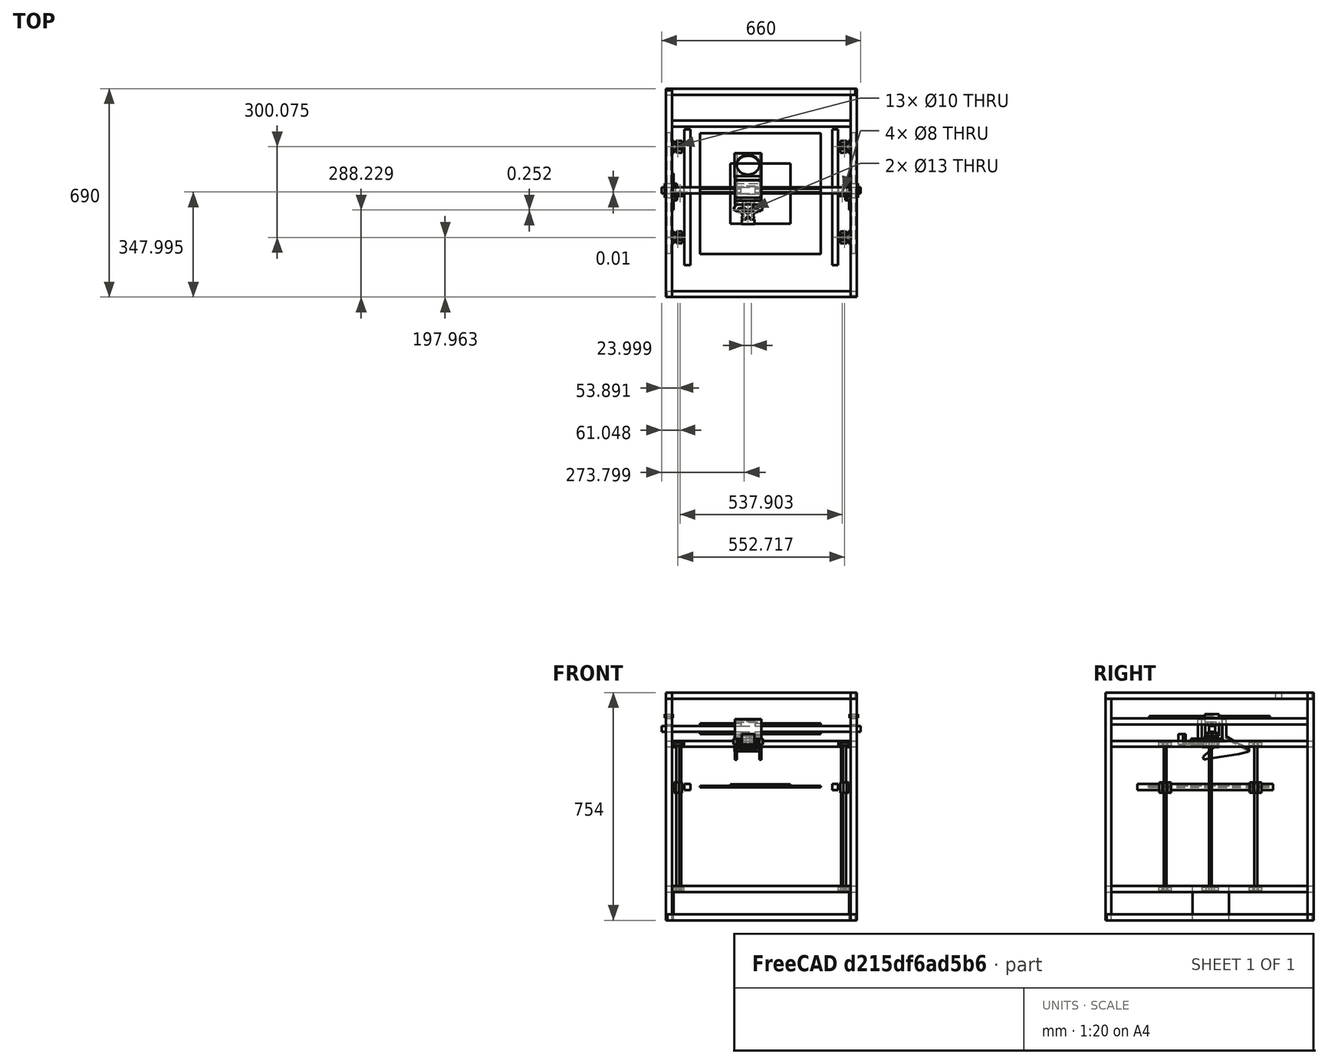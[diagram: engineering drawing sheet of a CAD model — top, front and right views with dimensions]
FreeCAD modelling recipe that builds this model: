
FCSTD DOCUMENT  (FreeCAD 0.17R13522 (Git))
Label: Frame_1
License: All rights reserved
LicenseURL: http://en.wikipedia.org/wiki/All_rights_reserved
objects: Part::Box×44, Sketcher::SketchObject×29, Part::Extrusion×29, Mesh::Feature×8, Part::Cylinder×6, Part::MultiFuse×3, App::DocumentObjectGroup×1
note: 111 computed .brp shape members not serialized (recipe doc carries the construction recipe); baked Part::Feature solids carry a one-line shape summary decoded from their .brp

FEATURE [Part::Box] Box017  label="Vslot Y Direito"
  AttacherType = Attacher::AttachEngine3D
  Height = 20
  Length = 20
  Placement = pos=(1268.5,175,-27.8) rot=(0,0,1;0rad)
  Width = 650
FEATURE [Part::Box] Box016  label="Vslot Y Esquerdo"
  AttacherType = Attacher::AttachEngine3D
  Height = 20
  Length = 20
  Placement = pos=(656,175,-27.8) rot=(0,0,1;0rad)
  Width = 650
FEATURE [Part::Box] Box020  label="Rail Y Esquerdo"
  AttacherType = Attacher::AttachEngine3D
  Height = 7.8
  Length = 12.2
  Placement = pos=(660,300,-7.8) rot=(0,0,1;0rad)
  Width = 400
FEATURE [Part::Box] Box021  label="Rail Y Direito"
  AttacherType = Attacher::AttachEngine3D
  Height = 7.8
  Length = 12.2
  Placement = pos=(1272.5,300,-7.8) rot=(0,0,1;0rad)
  Width = 400
FEATURE [Mesh::Feature] mgn12h_1  label="mgn12h_Esquerdo"
  Placement = pos=(690.5,535.45,17) rot=(-0.707107,0.707107,0;3.14159rad)
FEATURE [Mesh::Feature] mgn12h_002  label="mgn12h_Direito"
  Placement = pos=(1302,535.45,17) rot=(0.707107,-0.707107,0;3.14159rad)
FEATURE [Part::Box] Box005  label="Mgn12h y esquerdo"
  AttacherType = Attacher::AttachEngine3D
  Height = 13
  Length = 27.1
  Placement = pos=(652.5,484,-6) rot=(0,0,1;0rad)
  Width = 47.55
FEATURE [Part::Box] Box022  label="Mgn12h y direito"
  AttacherType = Attacher::AttachEngine3D
  Height = 13
  Length = 27.1
  Placement = pos=(1265,484,-6) rot=(0,0,1;0rad)
  Width = 47.55
FEATURE [Part::Box] Box  label="Vslot frontal esquerdo"
  AttacherType = Attacher::AttachEngine3D
  Height = 714
  Length = 20
  Placement = pos=(656,155,-656) rot=(0,0,1;0rad)
  Width = 20
FEATURE [Part::Box] Box023  label="Vslot frontal direito"
  AttacherType = Attacher::AttachEngine3D
  Height = 714
  Length = 20
  Placement = pos=(1268.5,155,-656) rot=(0,0,1;0rad)
  Width = 20
FEATURE [Part::Box] Box024  label="Vslot traseiro esquerdo"
  AttacherType = Attacher::AttachEngine3D
  Height = 714
  Length = 20
  Placement = pos=(656,825,-656) rot=(0,0,1;0rad)
  Width = 20
FEATURE [Part::Box] Box025  label="Vslot traseiro direito"
  AttacherType = Attacher::AttachEngine3D
  Height = 714
  Length = 20
  Placement = pos=(1268.5,825,-656) rot=(0,0,1;0rad)
  Width = 20
FEATURE [Part::Box] Box026  label="Vslot frontal inferior"
  AttacherType = Attacher::AttachEngine3D
  Height = 20
  Length = 607.5
  Placement = pos=(661,155,-676) rot=(0,0,1;0rad)
  Width = 20
FEATURE [Part::Box] Box027  label="Cantoneira front. Inf. Esquerda "
  AttacherType = Attacher::AttachEngine3D
  Height = 20
  Length = 5
  Placement = pos=(656,155,-676) rot=(0,0,1;0rad)
  Width = 20
FEATURE [Part::Box] Box028  label="Vslot Inferior Esquerdo"
  AttacherType = Attacher::AttachEngine3D
  Height = 20
  Length = 20
  Placement = pos=(656,175,-676) rot=(0,0,1;0rad)
  Width = 665
FEATURE [Part::Box] Box029  label="Cantoneira tras. Inf. Esquerda"
  AttacherType = Attacher::AttachEngine3D
  Height = 20
  Length = 20
  Placement = pos=(656,840,-676) rot=(0,0,1;0rad)
  Width = 5
FEATURE [Part::Box] Box030  label="Vslot traseiro inferior"
  AttacherType = Attacher::AttachEngine3D
  Height = 20
  Length = 607.5
  Placement = pos=(676,825,-676) rot=(0,0,1;0rad)
  Width = 20
FEATURE [Part::Box] Box032  label="Vslot Inferior Direito"
  AttacherType = Attacher::AttachEngine3D
  Height = 20
  Length = 20
  Placement = pos=(1268.5,160,-676) rot=(0,0,1;0rad)
  Width = 665
FEATURE [Part::Box] Box031  label="Cantoneira tras. inf. direita"
  AttacherType = Attacher::AttachEngine3D
  Height = 20
  Length = 5
  Placement = pos=(1283.5,825,-676) rot=(0,0,1;0rad)
  Width = 20
FEATURE [Part::Box] Box033  label="Cantoneira front. Inf. Direita"
  AttacherType = Attacher::AttachEngine3D
  Height = 20
  Length = 20
  Placement = pos=(1268.5,155,-676) rot=(0,0,1;0rad)
  Width = 5
FEATURE [Part::Box] Box034  label="Vslot inferior esquerdo"
  AttacherType = Attacher::AttachEngine3D
  Height = 20
  Length = 20
  Placement = pos=(656,155,58) rot=(0,0,1;0rad)
  Width = 685
FEATURE [Part::Box] Box036  label="Vslot superior direito"
  AttacherType = Attacher::AttachEngine3D
  Height = 20
  Length = 20
  Placement = pos=(1268.5,155,58) rot=(0,0,1;0rad)
  Width = 670
FEATURE [Part::Box] Box037  label="Vslot interno superior"
  AttacherType = Attacher::AttachEngine3D
  Height = 20
  Length = 592.5
  Placement = pos=(676,720,58) rot=(0,0,1;0rad)
  Width = 20
FEATURE [Part::Box] Box038  label="Cantoneira tras. sup. direita"
  AttacherType = Attacher::AttachEngine3D
  Height = 20
  Length = 5
  Placement = pos=(1283.5,825,58) rot=(0,0,1;0rad)
  Width = 20
FEATURE [Part::Box] Box039  label="Cantoneira tras. sup. esquerda"
  AttacherType = Attacher::AttachEngine3D
  Height = 20
  Length = 20
  Placement = pos=(656,840,58) rot=(0,0,1;0rad)
  Width = 5
FEATURE [Mesh::Feature] NEMA_17_Stepper_Motor_40mm  label="NEMA-17_CoreXY esquerdo"
  Placement = pos=(702,202,-22) rot=(0,0,1;0rad)
FEATURE [Mesh::Feature] NEMA_17_Stepper_Motor_40mm001  label="NEMA-17_CoreXY direito"
  Placement = pos=(1242,202,-22) rot=(0,0,1;0rad)
FEATURE [Mesh::Feature] NEMA_17_Stepper_Motor_40mm002  label="NEMA-17_Z esquerdo"
  Placement = pos=(703,503,-646) rot=(0,0,1;0rad)
FEATURE [Mesh::Feature] NEMA_17_Stepper_Motor_40mm003  label="NEMA-17_Z direito"
  Placement = pos=(1241,503,-646) rot=(0,0,1;0rad)
FEATURE [Part::Cylinder] Cylinder  label="Fuso Z direito"
  Angle = 360
  AttacherType = Attacher::AttachEngine3D
  Height = 500
  Placement = pos=(1241,503,-582) rot=(0,0,1;0rad)
  Radius = 4
FEATURE [Part::Cylinder] Cylinder001  label="Fuso Z esquerdo"
  Angle = 360
  AttacherType = Attacher::AttachEngine3D
  Height = 500
  Placement = pos=(703,503,-582) rot=(0,0,1;0rad)
  Radius = 4
FEATURE [Part::Box] Box040  label="Vslot Z sup. esquerdo"
  AttacherType = Attacher::AttachEngine3D
  Height = 20
  Length = 20
  Placement = pos=(656,175,-101.8) rot=(0,0,1;0rad)
  Width = 650
FEATURE [Part::Box] Box041  label="Vslot Z sup. direito"
  AttacherType = Attacher::AttachEngine3D
  Height = 20
  Length = 20
  Placement = pos=(1268.5,175,-101.8) rot=(0,0,1;0rad)
  Width = 650
FEATURE [Part::Box] Box042  label="Vslot traseiro superior"
  AttacherType = Attacher::AttachEngine3D
  Height = 20
  Length = 607.5
  Placement = pos=(676,825,58) rot=(0,0,1;0rad)
  Width = 20
FEATURE [Part::Box] Box043  label="Vslot frontal interno"
  AttacherType = Attacher::AttachEngine3D
  Height = 20
  Length = 592.5
  Placement = pos=(676,155,-582) rot=(0,0,1;0rad)
  Width = 20
FEATURE [Part::Box] Box044  label="Vslot traseiro interno inf."
  AttacherType = Attacher::AttachEngine3D
  Height = 20
  Length = 592.5
  Placement = pos=(676,825,-582) rot=(0,0,1;0rad)
  Width = 20
FEATURE [Part::Box] Box045  label="Vslot traseiro interno sup."
  AttacherType = Attacher::AttachEngine3D
  Height = 20
  Length = 592.5
  Placement = pos=(676,825,-101.8) rot=(0,0,1;0rad)
  Width = 20
FEATURE [Part::Box] Box046  label="Vslot Z inf. direito"
  AttacherType = Attacher::AttachEngine3D
  Height = 20
  Length = 20
  Placement = pos=(1268.5,175,-582) rot=(0,0,1;0rad)
  Width = 650
FEATURE [Part::Box] Box047  label="Vslot Z inf. esquerdo"
  AttacherType = Attacher::AttachEngine3D
  Height = 20
  Length = 20
  Placement = pos=(656,175,-582) rot=(0,0,1;0rad)
  Width = 650
FEATURE [Part::Cylinder] Cylinder002  label="Eixo Z esquerdo traseiro"
  Angle = 360
  AttacherType = Attacher::AttachEngine3D
  Height = 500
  Placement = pos=(696,653,-582) rot=(0,0,1;0rad)
  Radius = 5
FEATURE [Part::Cylinder] Cylinder003  label="Eixo Z esquerdo frontal"
  Angle = 360
  AttacherType = Attacher::AttachEngine3D
  Height = 500
  Placement = pos=(696,353,-582) rot=(0,0,1;0rad)
  Radius = 5
FEATURE [Part::Cylinder] Cylinder004  label="Eixo Z direito traseiro"
  Angle = 360
  AttacherType = Attacher::AttachEngine3D
  Height = 500
  Placement = pos=(1248.5,653,-582) rot=(0,0,1;0rad)
  Radius = 5
FEATURE [Part::Cylinder] Cylinder005  label="Eixo Z direito frontal"
  Angle = 360
  AttacherType = Attacher::AttachEngine3D
  Height = 500
  Placement = pos=(1248.5,353,-582) rot=(0,0,1;0rad)
  Radius = 5
FEATURE [Sketcher::SketchObject] Sketch
  sketch-geometry (9):
    g0: LineSegment StartX=28.5226 StartY=37.1384 StartZ=0 EndX=28.5226 EndY=43.1384 EndZ=0
    g1: LineSegment StartX=28.5226 StartY=43.1384 StartZ=0 EndX=40.5226 EndY=43.1384 EndZ=0
    g2: LineSegment StartX=40.5226 StartY=43.1384 StartZ=0 EndX=40.5226 EndY=70.1384 EndZ=0
    g3: LineSegment StartX=40.5226 StartY=70.1384 StartZ=0 EndX=58.5226 EndY=70.1384 EndZ=0
    g4: LineSegment StartX=58.5226 StartY=70.1384 StartZ=0 EndX=58.5226 EndY=43.1384 EndZ=0
    g5: LineSegment StartX=58.5226 StartY=43.1384 StartZ=0 EndX=70.5226 EndY=43.1384 EndZ=0
    g6: LineSegment StartX=70.5226 StartY=43.1384 StartZ=0 EndX=70.5226 EndY=37.1384 EndZ=0
    g7: LineSegment StartX=70.5226 StartY=37.1384 StartZ=0 EndX=28.5226 EndY=37.1384 EndZ=0
    g8: Circle CenterX=49.5226 CenterY=57.1384 CenterZ=0 NormalX=0 NormalY=0 NormalZ=1 AngleXU=0 Radius=5
  constraints (26):
    c: Vertical(g0)
    c: Coincident(g0,g1)
    c: Coincident(g1,g2)
    c: Vertical(g2)
    c: Coincident(g2,g3)
    c: Horizontal(g3)
    c: Coincident(g3,g4)
    c: Vertical(g4)
    c: Coincident(g4,g5)
    c: Coincident(g5,g6)
    c: Vertical(g6)
    c: Coincident(g6,g7)
    c: Coincident(g7,g0)
    c: Horizontal(g7)
    c: Horizontal(g1)
    c: Horizontal(g5)
    c: Equal(g0,g6)
    c: Equal(g2,g4)
    c: Equal(g1,g5)
    c: DistanceY(g0,g0) = 6
    c: DistanceY(g2,g2) = 27
    c: DistanceX(g3,g3) = 18
    c: DistanceX(g7,g7) = 42
    c: Radius(g8) = 5
    c: DistanceY(g8,g3) = 13
    c: DistanceX(g2,g8) = 9
FEATURE [Part::Extrusion] Extrude  label="SK10 sup. esquerdo frontal"
  Base = -> Sketch
  Dir = (0,0,14)
  DirMode = 0
  FaceMakerClass = Part::FaceMakerBullseye
  LengthFwd = 10
  LengthRev = 0
  Placement = pos=(639,402.5,-97) rot=(0,0,-1;1.5708rad)
  Solid = true
  Symmetric = false
FEATURE [Sketcher::SketchObject] Sketch001
  sketch-geometry (9):
    g0: LineSegment StartX=28.5226 StartY=37.1384 StartZ=0 EndX=28.5226 EndY=43.1384 EndZ=0
    g1: LineSegment StartX=28.5226 StartY=43.1384 StartZ=0 EndX=40.5226 EndY=43.1384 EndZ=0
    g2: LineSegment StartX=40.5226 StartY=43.1384 StartZ=0 EndX=40.5226 EndY=70.1384 EndZ=0
    g3: LineSegment StartX=40.5226 StartY=70.1384 StartZ=0 EndX=58.5226 EndY=70.1384 EndZ=0
    g4: LineSegment StartX=58.5226 StartY=70.1384 StartZ=0 EndX=58.5226 EndY=43.1384 EndZ=0
    g5: LineSegment StartX=58.5226 StartY=43.1384 StartZ=0 EndX=70.5226 EndY=43.1384 EndZ=0
    g6: LineSegment StartX=70.5226 StartY=43.1384 StartZ=0 EndX=70.5226 EndY=37.1384 EndZ=0
    g7: LineSegment StartX=70.5226 StartY=37.1384 StartZ=0 EndX=28.5226 EndY=37.1384 EndZ=0
    g8: Circle CenterX=49.5226 CenterY=57.1384 CenterZ=0 NormalX=0 NormalY=0 NormalZ=1 AngleXU=0 Radius=5
  constraints (26):
    c: Vertical(g0)
    c: Coincident(g0,g1)
    c: Coincident(g1,g2)
    c: Vertical(g2)
    c: Coincident(g2,g3)
    c: Horizontal(g3)
    c: Coincident(g3,g4)
    c: Vertical(g4)
    c: Coincident(g4,g5)
    c: Coincident(g5,g6)
    c: Vertical(g6)
    c: Coincident(g6,g7)
    c: Coincident(g7,g0)
    c: Horizontal(g7)
    c: Horizontal(g1)
    c: Horizontal(g5)
    c: Equal(g0,g6)
    c: Equal(g2,g4)
    c: Equal(g1,g5)
    c: DistanceY(g0,g0) = 6
    c: DistanceY(g2,g2) = 27
    c: DistanceX(g3,g3) = 18
    c: DistanceX(g7,g7) = 42
    c: Radius(g8) = 5
    c: DistanceY(g8,g3) = 13
    c: DistanceX(g2,g8) = 9
FEATURE [Part::Extrusion] Extrude001  label="SK10 sup. esquerdo traseiro"
  Base = -> Sketch001
  Dir = (0,0,14)
  DirMode = 0
  FaceMakerClass = Part::FaceMakerBullseye
  LengthFwd = 10
  LengthRev = 0
  Placement = pos=(639,702.5,-97) rot=(0,0,-1;1.5708rad)
  Solid = true
  Symmetric = false
FEATURE [Sketcher::SketchObject] Sketch002
  sketch-geometry (9):
    g0: LineSegment StartX=28.5226 StartY=37.1384 StartZ=0 EndX=28.5226 EndY=43.1384 EndZ=0
    g1: LineSegment StartX=28.5226 StartY=43.1384 StartZ=0 EndX=40.5226 EndY=43.1384 EndZ=0
    g2: LineSegment StartX=40.5226 StartY=43.1384 StartZ=0 EndX=40.5226 EndY=70.1384 EndZ=0
    g3: LineSegment StartX=40.5226 StartY=70.1384 StartZ=0 EndX=58.5226 EndY=70.1384 EndZ=0
    g4: LineSegment StartX=58.5226 StartY=70.1384 StartZ=0 EndX=58.5226 EndY=43.1384 EndZ=0
    g5: LineSegment StartX=58.5226 StartY=43.1384 StartZ=0 EndX=70.5226 EndY=43.1384 EndZ=0
    g6: LineSegment StartX=70.5226 StartY=43.1384 StartZ=0 EndX=70.5226 EndY=37.1384 EndZ=0
    g7: LineSegment StartX=70.5226 StartY=37.1384 StartZ=0 EndX=28.5226 EndY=37.1384 EndZ=0
    g8: Circle CenterX=49.5226 CenterY=57.1384 CenterZ=0 NormalX=0 NormalY=0 NormalZ=1 AngleXU=0 Radius=5
  constraints (26):
    c: Vertical(g0)
    c: Coincident(g0,g1)
    c: Coincident(g1,g2)
    c: Vertical(g2)
    c: Coincident(g2,g3)
    c: Horizontal(g3)
    c: Coincident(g3,g4)
    c: Vertical(g4)
    c: Coincident(g4,g5)
    c: Coincident(g5,g6)
    c: Vertical(g6)
    c: Coincident(g6,g7)
    c: Coincident(g7,g0)
    c: Horizontal(g7)
    c: Horizontal(g1)
    c: Horizontal(g5)
    c: Equal(g0,g6)
    c: Equal(g2,g4)
    c: Equal(g1,g5)
    c: DistanceY(g0,g0) = 6
    c: DistanceY(g2,g2) = 27
    c: DistanceX(g3,g3) = 18
    c: DistanceX(g7,g7) = 42
    c: Radius(g8) = 5
    c: DistanceY(g8,g3) = 13
    c: DistanceX(g2,g8) = 9
FEATURE [Part::Extrusion] Extrude002  label="SK10 inf. esquerdo traseiro"
  Base = -> Sketch002
  Dir = (0,0,14)
  DirMode = 0
  FaceMakerClass = Part::FaceMakerBullseye
  LengthFwd = 10
  LengthRev = 0
  Placement = pos=(639,702.5,-577) rot=(0,0,-1;1.5708rad)
  Solid = true
  Symmetric = false
FEATURE [Sketcher::SketchObject] Sketch003
  sketch-geometry (9):
    g0: LineSegment StartX=28.5226 StartY=37.1384 StartZ=0 EndX=28.5226 EndY=43.1384 EndZ=0
    g1: LineSegment StartX=28.5226 StartY=43.1384 StartZ=0 EndX=40.5226 EndY=43.1384 EndZ=0
    g2: LineSegment StartX=40.5226 StartY=43.1384 StartZ=0 EndX=40.5226 EndY=70.1384 EndZ=0
    g3: LineSegment StartX=40.5226 StartY=70.1384 StartZ=0 EndX=58.5226 EndY=70.1384 EndZ=0
    g4: LineSegment StartX=58.5226 StartY=70.1384 StartZ=0 EndX=58.5226 EndY=43.1384 EndZ=0
    g5: LineSegment StartX=58.5226 StartY=43.1384 StartZ=0 EndX=70.5226 EndY=43.1384 EndZ=0
    g6: LineSegment StartX=70.5226 StartY=43.1384 StartZ=0 EndX=70.5226 EndY=37.1384 EndZ=0
    g7: LineSegment StartX=70.5226 StartY=37.1384 StartZ=0 EndX=28.5226 EndY=37.1384 EndZ=0
    g8: Circle CenterX=49.5226 CenterY=57.1384 CenterZ=0 NormalX=0 NormalY=0 NormalZ=1 AngleXU=0 Radius=5
  constraints (26):
    c: Vertical(g0)
    c: Coincident(g0,g1)
    c: Coincident(g1,g2)
    c: Vertical(g2)
    c: Coincident(g2,g3)
    c: Horizontal(g3)
    c: Coincident(g3,g4)
    c: Vertical(g4)
    c: Coincident(g4,g5)
    c: Coincident(g5,g6)
    c: Vertical(g6)
    c: Coincident(g6,g7)
    c: Coincident(g7,g0)
    c: Horizontal(g7)
    c: Horizontal(g1)
    c: Horizontal(g5)
    c: Equal(g0,g6)
    c: Equal(g2,g4)
    c: Equal(g1,g5)
    c: DistanceY(g0,g0) = 6
    c: DistanceY(g2,g2) = 27
    c: DistanceX(g3,g3) = 18
    c: DistanceX(g7,g7) = 42
    c: Radius(g8) = 5
    c: DistanceY(g8,g3) = 13
    c: DistanceX(g2,g8) = 9
FEATURE [Part::Extrusion] Extrude003  label="SK10 inf. esquerdo frontal"
  Base = -> Sketch003
  Dir = (0,0,14)
  DirMode = 0
  FaceMakerClass = Part::FaceMakerBullseye
  LengthFwd = 10
  LengthRev = 0
  Placement = pos=(639,402.5,-577) rot=(0,0,-1;1.5708rad)
  Solid = true
  Symmetric = false
FEATURE [Sketcher::SketchObject] Sketch004
  sketch-geometry (9):
    g0: LineSegment StartX=28.5226 StartY=37.1384 StartZ=0 EndX=28.5226 EndY=43.1384 EndZ=0
    g1: LineSegment StartX=28.5226 StartY=43.1384 StartZ=0 EndX=40.5226 EndY=43.1384 EndZ=0
    g2: LineSegment StartX=40.5226 StartY=43.1384 StartZ=0 EndX=40.5226 EndY=70.1384 EndZ=0
    g3: LineSegment StartX=40.5226 StartY=70.1384 StartZ=0 EndX=58.5226 EndY=70.1384 EndZ=0
    g4: LineSegment StartX=58.5226 StartY=70.1384 StartZ=0 EndX=58.5226 EndY=43.1384 EndZ=0
    g5: LineSegment StartX=58.5226 StartY=43.1384 StartZ=0 EndX=70.5226 EndY=43.1384 EndZ=0
    g6: LineSegment StartX=70.5226 StartY=43.1384 StartZ=0 EndX=70.5226 EndY=37.1384 EndZ=0
    g7: LineSegment StartX=70.5226 StartY=37.1384 StartZ=0 EndX=28.5226 EndY=37.1384 EndZ=0
    g8: Circle CenterX=49.5226 CenterY=57.1384 CenterZ=0 NormalX=0 NormalY=0 NormalZ=1 AngleXU=0 Radius=5
  constraints (26):
    c: Vertical(g0)
    c: Coincident(g0,g1)
    c: Coincident(g1,g2)
    c: Vertical(g2)
    c: Coincident(g2,g3)
    c: Horizontal(g3)
    c: Coincident(g3,g4)
    c: Vertical(g4)
    c: Coincident(g4,g5)
    c: Coincident(g5,g6)
    c: Vertical(g6)
    c: Coincident(g6,g7)
    c: Coincident(g7,g0)
    c: Horizontal(g7)
    c: Horizontal(g1)
    c: Horizontal(g5)
    c: Equal(g0,g6)
    c: Equal(g2,g4)
    c: Equal(g1,g5)
    c: DistanceY(g0,g0) = 6
    c: DistanceY(g2,g2) = 27
    c: DistanceX(g3,g3) = 18
    c: DistanceX(g7,g7) = 42
    c: Radius(g8) = 5
    c: DistanceY(g8,g3) = 13
    c: DistanceX(g2,g8) = 9
FEATURE [Part::Extrusion] Extrude004  label="SK10 inf. direito frontal"
  Base = -> Sketch004
  Dir = (0,0,14)
  DirMode = 0
  FaceMakerClass = Part::FaceMakerBullseye
  LengthFwd = 10
  LengthRev = 0
  Placement = pos=(1305.5,303.5,-577) rot=(0,0,1;1.5708rad)
  Solid = true
  Symmetric = false
FEATURE [Sketcher::SketchObject] Sketch005
  sketch-geometry (9):
    g0: LineSegment StartX=28.5226 StartY=37.1384 StartZ=0 EndX=28.5226 EndY=43.1384 EndZ=0
    g1: LineSegment StartX=28.5226 StartY=43.1384 StartZ=0 EndX=40.5226 EndY=43.1384 EndZ=0
    g2: LineSegment StartX=40.5226 StartY=43.1384 StartZ=0 EndX=40.5226 EndY=70.1384 EndZ=0
    g3: LineSegment StartX=40.5226 StartY=70.1384 StartZ=0 EndX=58.5226 EndY=70.1384 EndZ=0
    g4: LineSegment StartX=58.5226 StartY=70.1384 StartZ=0 EndX=58.5226 EndY=43.1384 EndZ=0
    g5: LineSegment StartX=58.5226 StartY=43.1384 StartZ=0 EndX=70.5226 EndY=43.1384 EndZ=0
    g6: LineSegment StartX=70.5226 StartY=43.1384 StartZ=0 EndX=70.5226 EndY=37.1384 EndZ=0
    g7: LineSegment StartX=70.5226 StartY=37.1384 StartZ=0 EndX=28.5226 EndY=37.1384 EndZ=0
    g8: Circle CenterX=49.5226 CenterY=57.1384 CenterZ=0 NormalX=0 NormalY=0 NormalZ=1 AngleXU=0 Radius=5
  constraints (26):
    c: Vertical(g0)
    c: Coincident(g0,g1)
    c: Coincident(g1,g2)
    c: Vertical(g2)
    c: Coincident(g2,g3)
    c: Horizontal(g3)
    c: Coincident(g3,g4)
    c: Vertical(g4)
    c: Coincident(g4,g5)
    c: Coincident(g5,g6)
    c: Vertical(g6)
    c: Coincident(g6,g7)
    c: Coincident(g7,g0)
    c: Horizontal(g7)
    c: Horizontal(g1)
    c: Horizontal(g5)
    c: Equal(g0,g6)
    c: Equal(g2,g4)
    c: Equal(g1,g5)
    c: DistanceY(g0,g0) = 6
    c: DistanceY(g2,g2) = 27
    c: DistanceX(g3,g3) = 18
    c: DistanceX(g7,g7) = 42
    c: Radius(g8) = 5
    c: DistanceY(g8,g3) = 13
    c: DistanceX(g2,g8) = 9
FEATURE [Part::Extrusion] Extrude005  label="SK10 inf. direito traseiro"
  Base = -> Sketch005
  Dir = (0,0,14)
  DirMode = 0
  FaceMakerClass = Part::FaceMakerBullseye
  LengthFwd = 10
  LengthRev = 0
  Placement = pos=(1305.5,603.5,-577) rot=(0,0,1;1.5708rad)
  Solid = true
  Symmetric = false
FEATURE [Sketcher::SketchObject] Sketch006
  sketch-geometry (9):
    g0: LineSegment StartX=28.5226 StartY=37.1384 StartZ=0 EndX=28.5226 EndY=43.1384 EndZ=0
    g1: LineSegment StartX=28.5226 StartY=43.1384 StartZ=0 EndX=40.5226 EndY=43.1384 EndZ=0
    g2: LineSegment StartX=40.5226 StartY=43.1384 StartZ=0 EndX=40.5226 EndY=70.1384 EndZ=0
    g3: LineSegment StartX=40.5226 StartY=70.1384 StartZ=0 EndX=58.5226 EndY=70.1384 EndZ=0
    g4: LineSegment StartX=58.5226 StartY=70.1384 StartZ=0 EndX=58.5226 EndY=43.1384 EndZ=0
    g5: LineSegment StartX=58.5226 StartY=43.1384 StartZ=0 EndX=70.5226 EndY=43.1384 EndZ=0
    g6: LineSegment StartX=70.5226 StartY=43.1384 StartZ=0 EndX=70.5226 EndY=37.1384 EndZ=0
    g7: LineSegment StartX=70.5226 StartY=37.1384 StartZ=0 EndX=28.5226 EndY=37.1384 EndZ=0
    g8: Circle CenterX=49.5226 CenterY=57.1384 CenterZ=0 NormalX=0 NormalY=0 NormalZ=1 AngleXU=0 Radius=5
  constraints (26):
    c: Vertical(g0)
    c: Coincident(g0,g1)
    c: Coincident(g1,g2)
    c: Vertical(g2)
    c: Coincident(g2,g3)
    c: Horizontal(g3)
    c: Coincident(g3,g4)
    c: Vertical(g4)
    c: Coincident(g4,g5)
    c: Coincident(g5,g6)
    c: Vertical(g6)
    c: Coincident(g6,g7)
    c: Coincident(g7,g0)
    c: Horizontal(g7)
    c: Horizontal(g1)
    c: Horizontal(g5)
    c: Equal(g0,g6)
    c: Equal(g2,g4)
    c: Equal(g1,g5)
    c: DistanceY(g0,g0) = 6
    c: DistanceY(g2,g2) = 27
    c: DistanceX(g3,g3) = 18
    c: DistanceX(g7,g7) = 42
    c: Radius(g8) = 5
    c: DistanceY(g8,g3) = 13
    c: DistanceX(g2,g8) = 9
FEATURE [Part::Extrusion] Extrude006  label="SK10 sup. direito traseiro"
  Base = -> Sketch006
  Dir = (0,0,14)
  DirMode = 0
  FaceMakerClass = Part::FaceMakerBullseye
  LengthFwd = 10
  LengthRev = 0
  Placement = pos=(1305.5,603.5,-97) rot=(0,0,1;1.5708rad)
  Solid = true
  Symmetric = false
FEATURE [Sketcher::SketchObject] Sketch007
  sketch-geometry (9):
    g0: LineSegment StartX=28.5226 StartY=37.1384 StartZ=0 EndX=28.5226 EndY=43.1384 EndZ=0
    g1: LineSegment StartX=28.5226 StartY=43.1384 StartZ=0 EndX=40.5226 EndY=43.1384 EndZ=0
    g2: LineSegment StartX=40.5226 StartY=43.1384 StartZ=0 EndX=40.5226 EndY=70.1384 EndZ=0
    g3: LineSegment StartX=40.5226 StartY=70.1384 StartZ=0 EndX=58.5226 EndY=70.1384 EndZ=0
    g4: LineSegment StartX=58.5226 StartY=70.1384 StartZ=0 EndX=58.5226 EndY=43.1384 EndZ=0
    g5: LineSegment StartX=58.5226 StartY=43.1384 StartZ=0 EndX=70.5226 EndY=43.1384 EndZ=0
    g6: LineSegment StartX=70.5226 StartY=43.1384 StartZ=0 EndX=70.5226 EndY=37.1384 EndZ=0
    g7: LineSegment StartX=70.5226 StartY=37.1384 StartZ=0 EndX=28.5226 EndY=37.1384 EndZ=0
    g8: Circle CenterX=49.5226 CenterY=57.1384 CenterZ=0 NormalX=0 NormalY=0 NormalZ=1 AngleXU=0 Radius=5
  constraints (26):
    c: Vertical(g0)
    c: Coincident(g0,g1)
    c: Coincident(g1,g2)
    c: Vertical(g2)
    c: Coincident(g2,g3)
    c: Horizontal(g3)
    c: Coincident(g3,g4)
    c: Vertical(g4)
    c: Coincident(g4,g5)
    c: Coincident(g5,g6)
    c: Vertical(g6)
    c: Coincident(g6,g7)
    c: Coincident(g7,g0)
    c: Horizontal(g7)
    c: Horizontal(g1)
    c: Horizontal(g5)
    c: Equal(g0,g6)
    c: Equal(g2,g4)
    c: Equal(g1,g5)
    c: DistanceY(g0,g0) = 6
    c: DistanceY(g2,g2) = 27
    c: DistanceX(g3,g3) = 18
    c: DistanceX(g7,g7) = 42
    c: Radius(g8) = 5
    c: DistanceY(g8,g3) = 13
    c: DistanceX(g2,g8) = 9
FEATURE [Part::Extrusion] Extrude007  label="SK10 sup. direito frontal"
  Base = -> Sketch007
  Dir = (0,0,14)
  DirMode = 0
  FaceMakerClass = Part::FaceMakerBullseye
  LengthFwd = 10
  LengthRev = 0
  Placement = pos=(1305.5,303.5,-97) rot=(0,0,1;1.5708rad)
  Solid = true
  Symmetric = false
FEATURE [Sketcher::SketchObject] Sketch008
  sketch-geometry (17):
    g0: LineSegment StartX=35.5374 StartY=23.1087 StartZ=0 EndX=35.5374 EndY=33.1087 EndZ=0
    g1: LineSegment StartX=35.5374 StartY=33.1087 StartZ=0 EndX=36.5374 EndY=33.1087 EndZ=0
    g2: LineSegment StartX=36.5374 StartY=33.1087 StartZ=0 EndX=36.5374 EndY=44.1087 EndZ=0
    g3: LineSegment StartX=36.5374 StartY=44.1087 StartZ=0 EndX=46.5374 EndY=44.1087 EndZ=0
    g4: LineSegment StartX=46.5374 StartY=44.1087 StartZ=0 EndX=50.6224 EndY=50.1087 EndZ=0
    g5: LineSegment StartX=50.6224 StartY=50.1087 StartZ=0 EndX=60.6224 EndY=50.1087 EndZ=0
    g6: LineSegment StartX=60.6224 StartY=50.1087 StartZ=0 EndX=64.5374 EndY=44.1087 EndZ=0
    g7: LineSegment StartX=64.5374 StartY=44.1087 StartZ=0 EndX=74.5374 EndY=44.1087 EndZ=0
    g8: LineSegment StartX=74.5374 StartY=44.1087 StartZ=0 EndX=74.5374 EndY=33.1087 EndZ=0
    g9: LineSegment StartX=74.5374 StartY=33.1087 StartZ=0 EndX=75.5374 EndY=33.1087 EndZ=0
    g10: LineSegment StartX=75.5374 StartY=33.1087 StartZ=0 EndX=75.5374 EndY=23.1087 EndZ=0
    g11: LineSegment StartX=75.5374 StartY=23.1087 StartZ=0 EndX=64.5374 EndY=23.1087 EndZ=0
    g12: LineSegment StartX=64.5374 StartY=23.1087 StartZ=0 EndX=64.5374 EndY=24.1087 EndZ=0
    g13: LineSegment StartX=64.5374 StartY=24.1087 StartZ=0 EndX=46.5374 EndY=24.1087 EndZ=0
    g14: LineSegment StartX=46.5374 StartY=24.1087 StartZ=0 EndX=46.5374 EndY=23.1087 EndZ=0
    g15: LineSegment StartX=46.5374 StartY=23.1087 StartZ=0 EndX=35.5374 EndY=23.1087 EndZ=0
    g16: Circle CenterX=55.5374 CenterY=37.1087 CenterZ=0 NormalX=0 NormalY=0 NormalZ=1 AngleXU=0 Radius=5
  constraints (48):
    c: Coincident(g0,g1)
    c: Coincident(g1,g2)
    c: Vertical(g2)
    c: Coincident(g2,g3)
    c: Horizontal(g3)
    c: Coincident(g3,g4)
    c: Coincident(g4,g5)
    c: Horizontal(g5)
    c: Coincident(g5,g6)
    c: Coincident(g6,g7)
    c: Horizontal(g7)
    c: Coincident(g7,g8)
    c: Vertical(g8)
    c: Coincident(g8,g9)
    c: Coincident(g9,g10)
    c: Vertical(g10)
    c: Coincident(g10,g11)
    c: Horizontal(g11)
    c: Coincident(g11,g12)
    c: Coincident(g12,g13)
    c: Horizontal(g13)
    c: Coincident(g13,g14)
    c: Vertical(g14)
    c: Coincident(g14,g15)
    c: Coincident(g15,g0)
    c: Horizontal(g15)
    c: Horizontal(g1)
    c: Horizontal(g9)
    c: Vertical(g0)
    c: Vertical(g12)
    c: DistanceX(g11,g11) = 11
    c: Equal(g11,g15)
    c: DistanceY(g10,g10) = 10
    c: Equal(g0,g10)
    c: DistanceY(g8,g8) = 11
    c: Equal(g8,g2)
    c: DistanceX(g13,g13) = 18
    c: DistanceY(g12,g12) = 1
    c: Equal(g12,g14)
    c: DistanceX(g1,g1) = 1
    c: Equal(g1,g9)
    c: DistanceX(g5,g5) = 10
    c: DistanceX(g3,g3) = 10
    c: Equal(g3,g7)
    c: DistanceY(g6,g6) = 6
    c: Radius(g16) = 5
    c: Distance(g16,g5) = 13
    c: Distance(g16,g2) = 19
FEATURE [Part::Extrusion] Extrude008  label="SC10UU Z esquerdo frontal"
  Base = -> Sketch008
  Dir = (0,0,1)
  DirMode = 2
  FaceMakerClass = Part::FaceMakerBullseye
  LengthFwd = 35
  LengthRev = 0
  Placement = pos=(733,297.5,-254) rot=(0,0,1;1.5708rad)
  Solid = true
  Symmetric = false
FEATURE [Sketcher::SketchObject] Sketch009
  sketch-geometry (17):
    g0: LineSegment StartX=35.5374 StartY=23.1087 StartZ=0 EndX=35.5374 EndY=33.1087 EndZ=0
    g1: LineSegment StartX=35.5374 StartY=33.1087 StartZ=0 EndX=36.5374 EndY=33.1087 EndZ=0
    g2: LineSegment StartX=36.5374 StartY=33.1087 StartZ=0 EndX=36.5374 EndY=44.1087 EndZ=0
    g3: LineSegment StartX=36.5374 StartY=44.1087 StartZ=0 EndX=46.5374 EndY=44.1087 EndZ=0
    g4: LineSegment StartX=46.5374 StartY=44.1087 StartZ=0 EndX=50.6224 EndY=50.1087 EndZ=0
    g5: LineSegment StartX=50.6224 StartY=50.1087 StartZ=0 EndX=60.6224 EndY=50.1087 EndZ=0
    g6: LineSegment StartX=60.6224 StartY=50.1087 StartZ=0 EndX=64.5374 EndY=44.1087 EndZ=0
    g7: LineSegment StartX=64.5374 StartY=44.1087 StartZ=0 EndX=74.5374 EndY=44.1087 EndZ=0
    g8: LineSegment StartX=74.5374 StartY=44.1087 StartZ=0 EndX=74.5374 EndY=33.1087 EndZ=0
    g9: LineSegment StartX=74.5374 StartY=33.1087 StartZ=0 EndX=75.5374 EndY=33.1087 EndZ=0
    g10: LineSegment StartX=75.5374 StartY=33.1087 StartZ=0 EndX=75.5374 EndY=23.1087 EndZ=0
    g11: LineSegment StartX=75.5374 StartY=23.1087 StartZ=0 EndX=64.5374 EndY=23.1087 EndZ=0
    g12: LineSegment StartX=64.5374 StartY=23.1087 StartZ=0 EndX=64.5374 EndY=24.1087 EndZ=0
    g13: LineSegment StartX=64.5374 StartY=24.1087 StartZ=0 EndX=46.5374 EndY=24.1087 EndZ=0
    g14: LineSegment StartX=46.5374 StartY=24.1087 StartZ=0 EndX=46.5374 EndY=23.1087 EndZ=0
    g15: LineSegment StartX=46.5374 StartY=23.1087 StartZ=0 EndX=35.5374 EndY=23.1087 EndZ=0
    g16: Circle CenterX=55.5374 CenterY=37.1087 CenterZ=0 NormalX=0 NormalY=0 NormalZ=1 AngleXU=0 Radius=5
  constraints (48):
    c: Coincident(g0,g1)
    c: Coincident(g1,g2)
    c: Vertical(g2)
    c: Coincident(g2,g3)
    c: Horizontal(g3)
    c: Coincident(g3,g4)
    c: Coincident(g4,g5)
    c: Horizontal(g5)
    c: Coincident(g5,g6)
    c: Coincident(g6,g7)
    c: Horizontal(g7)
    c: Coincident(g7,g8)
    c: Vertical(g8)
    c: Coincident(g8,g9)
    c: Coincident(g9,g10)
    c: Vertical(g10)
    c: Coincident(g10,g11)
    c: Horizontal(g11)
    c: Coincident(g11,g12)
    c: Coincident(g12,g13)
    c: Horizontal(g13)
    c: Coincident(g13,g14)
    c: Vertical(g14)
    c: Coincident(g14,g15)
    c: Coincident(g15,g0)
    c: Horizontal(g15)
    c: Horizontal(g1)
    c: Horizontal(g9)
    c: Vertical(g0)
    c: Vertical(g12)
    c: DistanceX(g11,g11) = 11
    c: Equal(g11,g15)
    c: DistanceY(g10,g10) = 10
    c: Equal(g0,g10)
    c: DistanceY(g8,g8) = 11
    c: Equal(g8,g2)
    c: DistanceX(g13,g13) = 18
    c: DistanceY(g12,g12) = 1
    c: Equal(g12,g14)
    c: DistanceX(g1,g1) = 1
    c: Equal(g1,g9)
    c: DistanceX(g5,g5) = 10
    c: DistanceX(g3,g3) = 10
    c: Equal(g3,g7)
    c: DistanceY(g6,g6) = 6
    c: Radius(g16) = 5
    c: Distance(g16,g5) = 13
    c: Distance(g16,g2) = 19
FEATURE [Part::Extrusion] Extrude009  label="SC10UU Z direito traseiro"
  Base = -> Sketch009
  Dir = (0,0,1)
  DirMode = 2
  FaceMakerClass = Part::FaceMakerBullseye
  LengthFwd = 35
  LengthRev = 0
  Placement = pos=(1211.5,708.5,-254) rot=(0,0,-1;1.5708rad)
  Solid = true
  Symmetric = false
FEATURE [Sketcher::SketchObject] Sketch010
  sketch-geometry (17):
    g0: LineSegment StartX=35.5374 StartY=23.1087 StartZ=0 EndX=35.5374 EndY=33.1087 EndZ=0
    g1: LineSegment StartX=35.5374 StartY=33.1087 StartZ=0 EndX=36.5374 EndY=33.1087 EndZ=0
    g2: LineSegment StartX=36.5374 StartY=33.1087 StartZ=0 EndX=36.5374 EndY=44.1087 EndZ=0
    g3: LineSegment StartX=36.5374 StartY=44.1087 StartZ=0 EndX=46.5374 EndY=44.1087 EndZ=0
    g4: LineSegment StartX=46.5374 StartY=44.1087 StartZ=0 EndX=50.6224 EndY=50.1087 EndZ=0
    g5: LineSegment StartX=50.6224 StartY=50.1087 StartZ=0 EndX=60.6224 EndY=50.1087 EndZ=0
    g6: LineSegment StartX=60.6224 StartY=50.1087 StartZ=0 EndX=64.5374 EndY=44.1087 EndZ=0
    g7: LineSegment StartX=64.5374 StartY=44.1087 StartZ=0 EndX=74.5374 EndY=44.1087 EndZ=0
    g8: LineSegment StartX=74.5374 StartY=44.1087 StartZ=0 EndX=74.5374 EndY=33.1087 EndZ=0
    g9: LineSegment StartX=74.5374 StartY=33.1087 StartZ=0 EndX=75.5374 EndY=33.1087 EndZ=0
    g10: LineSegment StartX=75.5374 StartY=33.1087 StartZ=0 EndX=75.5374 EndY=23.1087 EndZ=0
    g11: LineSegment StartX=75.5374 StartY=23.1087 StartZ=0 EndX=64.5374 EndY=23.1087 EndZ=0
    g12: LineSegment StartX=64.5374 StartY=23.1087 StartZ=0 EndX=64.5374 EndY=24.1087 EndZ=0
    g13: LineSegment StartX=64.5374 StartY=24.1087 StartZ=0 EndX=46.5374 EndY=24.1087 EndZ=0
    g14: LineSegment StartX=46.5374 StartY=24.1087 StartZ=0 EndX=46.5374 EndY=23.1087 EndZ=0
    g15: LineSegment StartX=46.5374 StartY=23.1087 StartZ=0 EndX=35.5374 EndY=23.1087 EndZ=0
    g16: Circle CenterX=55.5374 CenterY=37.1087 CenterZ=0 NormalX=0 NormalY=0 NormalZ=1 AngleXU=0 Radius=5
  constraints (48):
    c: Coincident(g0,g1)
    c: Coincident(g1,g2)
    c: Vertical(g2)
    c: Coincident(g2,g3)
    c: Horizontal(g3)
    c: Coincident(g3,g4)
    c: Coincident(g4,g5)
    c: Horizontal(g5)
    c: Coincident(g5,g6)
    c: Coincident(g6,g7)
    c: Horizontal(g7)
    c: Coincident(g7,g8)
    c: Vertical(g8)
    c: Coincident(g8,g9)
    c: Coincident(g9,g10)
    c: Vertical(g10)
    c: Coincident(g10,g11)
    c: Horizontal(g11)
    c: Coincident(g11,g12)
    c: Coincident(g12,g13)
    c: Horizontal(g13)
    c: Coincident(g13,g14)
    c: Vertical(g14)
    c: Coincident(g14,g15)
    c: Coincident(g15,g0)
    c: Horizontal(g15)
    c: Horizontal(g1)
    c: Horizontal(g9)
    c: Vertical(g0)
    c: Vertical(g12)
    c: DistanceX(g11,g11) = 11
    c: Equal(g11,g15)
    c: DistanceY(g10,g10) = 10
    c: Equal(g0,g10)
    c: DistanceY(g8,g8) = 11
    c: Equal(g8,g2)
    c: DistanceX(g13,g13) = 18
    c: DistanceY(g12,g12) = 1
    c: Equal(g12,g14)
    c: DistanceX(g1,g1) = 1
    c: Equal(g1,g9)
    c: DistanceX(g5,g5) = 10
    c: DistanceX(g3,g3) = 10
    c: Equal(g3,g7)
    c: DistanceY(g6,g6) = 6
    c: Radius(g16) = 5
    c: Distance(g16,g5) = 13
    c: Distance(g16,g2) = 19
FEATURE [Part::Extrusion] Extrude010  label="SC10UU Z direito frontal"
  Base = -> Sketch010
  Dir = (0,0,1)
  DirMode = 2
  FaceMakerClass = Part::FaceMakerBullseye
  LengthFwd = 35
  LengthRev = 0
  Placement = pos=(1211.5,408.5,-254) rot=(0,0,-1;1.5708rad)
  Solid = true
  Symmetric = false
FEATURE [Sketcher::SketchObject] Sketch011
  sketch-geometry (17):
    g0: LineSegment StartX=35.5374 StartY=23.1087 StartZ=0 EndX=35.5374 EndY=33.1087 EndZ=0
    g1: LineSegment StartX=35.5374 StartY=33.1087 StartZ=0 EndX=36.5374 EndY=33.1087 EndZ=0
    g2: LineSegment StartX=36.5374 StartY=33.1087 StartZ=0 EndX=36.5374 EndY=44.1087 EndZ=0
    g3: LineSegment StartX=36.5374 StartY=44.1087 StartZ=0 EndX=46.5374 EndY=44.1087 EndZ=0
    g4: LineSegment StartX=46.5374 StartY=44.1087 StartZ=0 EndX=50.6224 EndY=50.1087 EndZ=0
    g5: LineSegment StartX=50.6224 StartY=50.1087 StartZ=0 EndX=60.6224 EndY=50.1087 EndZ=0
    g6: LineSegment StartX=60.6224 StartY=50.1087 StartZ=0 EndX=64.5374 EndY=44.1087 EndZ=0
    g7: LineSegment StartX=64.5374 StartY=44.1087 StartZ=0 EndX=74.5374 EndY=44.1087 EndZ=0
    g8: LineSegment StartX=74.5374 StartY=44.1087 StartZ=0 EndX=74.5374 EndY=33.1087 EndZ=0
    g9: LineSegment StartX=74.5374 StartY=33.1087 StartZ=0 EndX=75.5374 EndY=33.1087 EndZ=0
    g10: LineSegment StartX=75.5374 StartY=33.1087 StartZ=0 EndX=75.5374 EndY=23.1087 EndZ=0
    g11: LineSegment StartX=75.5374 StartY=23.1087 StartZ=0 EndX=64.5374 EndY=23.1087 EndZ=0
    g12: LineSegment StartX=64.5374 StartY=23.1087 StartZ=0 EndX=64.5374 EndY=24.1087 EndZ=0
    g13: LineSegment StartX=64.5374 StartY=24.1087 StartZ=0 EndX=46.5374 EndY=24.1087 EndZ=0
    g14: LineSegment StartX=46.5374 StartY=24.1087 StartZ=0 EndX=46.5374 EndY=23.1087 EndZ=0
    g15: LineSegment StartX=46.5374 StartY=23.1087 StartZ=0 EndX=35.5374 EndY=23.1087 EndZ=0
    g16: Circle CenterX=55.5374 CenterY=37.1087 CenterZ=0 NormalX=0 NormalY=0 NormalZ=1 AngleXU=0 Radius=5
  constraints (48):
    c: Coincident(g0,g1)
    c: Coincident(g1,g2)
    c: Vertical(g2)
    c: Coincident(g2,g3)
    c: Horizontal(g3)
    c: Coincident(g3,g4)
    c: Coincident(g4,g5)
    c: Horizontal(g5)
    c: Coincident(g5,g6)
    c: Coincident(g6,g7)
    c: Horizontal(g7)
    c: Coincident(g7,g8)
    c: Vertical(g8)
    c: Coincident(g8,g9)
    c: Coincident(g9,g10)
    c: Vertical(g10)
    c: Coincident(g10,g11)
    c: Horizontal(g11)
    c: Coincident(g11,g12)
    c: Coincident(g12,g13)
    c: Horizontal(g13)
    c: Coincident(g13,g14)
    c: Vertical(g14)
    c: Coincident(g14,g15)
    c: Coincident(g15,g0)
    c: Horizontal(g15)
    c: Horizontal(g1)
    c: Horizontal(g9)
    c: Vertical(g0)
    c: Vertical(g12)
    c: DistanceX(g11,g11) = 11
    c: Equal(g11,g15)
    c: DistanceY(g10,g10) = 10
    c: Equal(g0,g10)
    c: DistanceY(g8,g8) = 11
    c: Equal(g8,g2)
    c: DistanceX(g13,g13) = 18
    c: DistanceY(g12,g12) = 1
    c: Equal(g12,g14)
    c: DistanceX(g1,g1) = 1
    c: Equal(g1,g9)
    c: DistanceX(g5,g5) = 10
    c: DistanceX(g3,g3) = 10
    c: Equal(g3,g7)
    c: DistanceY(g6,g6) = 6
    c: Radius(g16) = 5
    c: Distance(g16,g5) = 13
    c: Distance(g16,g2) = 19
FEATURE [Part::Extrusion] Extrude011  label="SC10UU Z esquerdo traseiro"
  Base = -> Sketch011
  Dir = (0,0,1)
  DirMode = 2
  FaceMakerClass = Part::FaceMakerBullseye
  LengthFwd = 35
  LengthRev = 0
  Placement = pos=(733,597.5,-254) rot=(0,0,1;1.5708rad)
  Solid = true
  Symmetric = false
FEATURE [Sketcher::SketchObject] Sketch012
  sketch-geometry (9):
    g0: LineSegment StartX=16.0483 StartY=60.995 StartZ=0 EndX=16.0483 EndY=5.99503 EndZ=0
    g1: LineSegment StartX=16.0483 StartY=5.99503 StartZ=0 EndX=21.0483 EndY=5.99503 EndZ=0
    g2: LineSegment StartX=21.0483 StartY=5.99503 StartZ=0 EndX=21.0483 EndY=19.995 EndZ=0
    g3: LineSegment StartX=21.0483 StartY=19.995 StartZ=0 EndX=44.5483 EndY=19.995 EndZ=0
    g4: LineSegment StartX=44.5483 StartY=19.995 StartZ=0 EndX=44.5483 EndY=46.995 EndZ=0
    g5: LineSegment StartX=44.5483 StartY=46.995 StartZ=0 EndX=21.0483 EndY=46.995 EndZ=0
    g6: LineSegment StartX=21.0483 StartY=46.995 StartZ=0 EndX=21.0483 EndY=60.995 EndZ=0
    g7: LineSegment StartX=21.0483 StartY=60.995 StartZ=0 EndX=16.0483 EndY=60.995 EndZ=0
    g8: Circle CenterX=31.0483 CenterY=33.495 CenterZ=0 NormalX=0 NormalY=0 NormalZ=1 AngleXU=0 Radius=4
  constraints (25):
    c: Vertical(g0)
    c: Coincident(g0,g1)
    c: Horizontal(g1)
    c: Coincident(g1,g2)
    c: Vertical(g2)
    c: Coincident(g2,g3)
    c: Horizontal(g3)
    c: Coincident(g3,g4)
    c: Vertical(g4)
    c: Coincident(g4,g5)
    c: Horizontal(g5)
    c: Coincident(g5,g6)
    c: Vertical(g6)
    c: Coincident(g6,g7)
    c: Coincident(g7,g0)
    c: Horizontal(g7)
    c: DistanceY(g0,g0) = 55
    c: DistanceX(g7,g7) = 5
    c: Equal(g7,g1)
    c: Radius(g8) = 4
    c: Distance(g8,g0) = 15
    c: Equal(g6,g2)
    c: Distance(g8,g4) = 13.5
    c: Distance(g8,g5) = 13.5
    c: Distance(g8,g3) = 13.5
FEATURE [Part::Extrusion] Extrude012  label="KP08 Z sup. esquerdo"
  Base = -> Sketch012
  Dir = (0,0,13)
  DirMode = 0
  FaceMakerClass = Part::FaceMakerBullseye
  LengthFwd = 10
  LengthRev = 0
  Placement = pos=(672,469.5,-97) rot=(0,0,1;0rad)
  Solid = true
  Symmetric = false
FEATURE [Sketcher::SketchObject] Sketch013
  sketch-geometry (9):
    g0: LineSegment StartX=16.0483 StartY=60.995 StartZ=0 EndX=16.0483 EndY=5.99503 EndZ=0
    g1: LineSegment StartX=16.0483 StartY=5.99503 StartZ=0 EndX=21.0483 EndY=5.99503 EndZ=0
    g2: LineSegment StartX=21.0483 StartY=5.99503 StartZ=0 EndX=21.0483 EndY=19.995 EndZ=0
    g3: LineSegment StartX=21.0483 StartY=19.995 StartZ=0 EndX=44.5483 EndY=19.995 EndZ=0
    g4: LineSegment StartX=44.5483 StartY=19.995 StartZ=0 EndX=44.5483 EndY=46.995 EndZ=0
    g5: LineSegment StartX=44.5483 StartY=46.995 StartZ=0 EndX=21.0483 EndY=46.995 EndZ=0
    g6: LineSegment StartX=21.0483 StartY=46.995 StartZ=0 EndX=21.0483 EndY=60.995 EndZ=0
    g7: LineSegment StartX=21.0483 StartY=60.995 StartZ=0 EndX=16.0483 EndY=60.995 EndZ=0
    g8: Circle CenterX=31.0483 CenterY=33.495 CenterZ=0 NormalX=0 NormalY=0 NormalZ=1 AngleXU=0 Radius=4
  constraints (25):
    c: Vertical(g0)
    c: Coincident(g0,g1)
    c: Horizontal(g1)
    c: Coincident(g1,g2)
    c: Vertical(g2)
    c: Coincident(g2,g3)
    c: Horizontal(g3)
    c: Coincident(g3,g4)
    c: Vertical(g4)
    c: Coincident(g4,g5)
    c: Horizontal(g5)
    c: Coincident(g5,g6)
    c: Vertical(g6)
    c: Coincident(g6,g7)
    c: Coincident(g7,g0)
    c: Horizontal(g7)
    c: DistanceY(g0,g0) = 55
    c: DistanceX(g7,g7) = 5
    c: Equal(g7,g1)
    c: Radius(g8) = 4
    c: Distance(g8,g0) = 15
    c: Equal(g6,g2)
    c: Distance(g8,g4) = 13.5
    c: Distance(g8,g5) = 13.5
    c: Distance(g8,g3) = 13.5
FEATURE [Part::Extrusion] Extrude013  label="KP08 Z inf. esquerdo"
  Base = -> Sketch013
  Dir = (0,0,13)
  DirMode = 0
  FaceMakerClass = Part::FaceMakerBullseye
  LengthFwd = 10
  LengthRev = 0
  Placement = pos=(672,469.5,-577) rot=(0,0,1;0rad)
  Solid = true
  Symmetric = false
FEATURE [Sketcher::SketchObject] Sketch014
  sketch-geometry (9):
    g0: LineSegment StartX=16.0483 StartY=60.995 StartZ=0 EndX=16.0483 EndY=5.99503 EndZ=0
    g1: LineSegment StartX=16.0483 StartY=5.99503 StartZ=0 EndX=21.0483 EndY=5.99503 EndZ=0
    g2: LineSegment StartX=21.0483 StartY=5.99503 StartZ=0 EndX=21.0483 EndY=19.995 EndZ=0
    g3: LineSegment StartX=21.0483 StartY=19.995 StartZ=0 EndX=44.5483 EndY=19.995 EndZ=0
    g4: LineSegment StartX=44.5483 StartY=19.995 StartZ=0 EndX=44.5483 EndY=46.995 EndZ=0
    g5: LineSegment StartX=44.5483 StartY=46.995 StartZ=0 EndX=21.0483 EndY=46.995 EndZ=0
    g6: LineSegment StartX=21.0483 StartY=46.995 StartZ=0 EndX=21.0483 EndY=60.995 EndZ=0
    g7: LineSegment StartX=21.0483 StartY=60.995 StartZ=0 EndX=16.0483 EndY=60.995 EndZ=0
    g8: Circle CenterX=31.0483 CenterY=33.495 CenterZ=0 NormalX=0 NormalY=0 NormalZ=1 AngleXU=0 Radius=4
  constraints (25):
    c: Vertical(g0)
    c: Coincident(g0,g1)
    c: Horizontal(g1)
    c: Coincident(g1,g2)
    c: Vertical(g2)
    c: Coincident(g2,g3)
    c: Horizontal(g3)
    c: Coincident(g3,g4)
    c: Vertical(g4)
    c: Coincident(g4,g5)
    c: Horizontal(g5)
    c: Coincident(g5,g6)
    c: Vertical(g6)
    c: Coincident(g6,g7)
    c: Coincident(g7,g0)
    c: Horizontal(g7)
    c: DistanceY(g0,g0) = 55
    c: DistanceX(g7,g7) = 5
    c: Equal(g7,g1)
    c: Radius(g8) = 4
    c: Distance(g8,g0) = 15
    c: Equal(g6,g2)
    c: Distance(g8,g4) = 13.5
    c: Distance(g8,g5) = 13.5
    c: Distance(g8,g3) = 13.5
FEATURE [Part::Extrusion] Extrude014  label="KP08 Z inf. direito"
  Base = -> Sketch014
  Dir = (0,0,13)
  DirMode = 0
  FaceMakerClass = Part::FaceMakerBullseye
  LengthFwd = 10
  LengthRev = 0
  Placement = pos=(1272,536.5,-577) rot=(0,0,1;3.14159rad)
  Solid = true
  Symmetric = false
FEATURE [Sketcher::SketchObject] Sketch015
  sketch-geometry (9):
    g0: LineSegment StartX=16.0483 StartY=60.995 StartZ=0 EndX=16.0483 EndY=5.99503 EndZ=0
    g1: LineSegment StartX=16.0483 StartY=5.99503 StartZ=0 EndX=21.0483 EndY=5.99503 EndZ=0
    g2: LineSegment StartX=21.0483 StartY=5.99503 StartZ=0 EndX=21.0483 EndY=19.995 EndZ=0
    g3: LineSegment StartX=21.0483 StartY=19.995 StartZ=0 EndX=44.5483 EndY=19.995 EndZ=0
    g4: LineSegment StartX=44.5483 StartY=19.995 StartZ=0 EndX=44.5483 EndY=46.995 EndZ=0
    g5: LineSegment StartX=44.5483 StartY=46.995 StartZ=0 EndX=21.0483 EndY=46.995 EndZ=0
    g6: LineSegment StartX=21.0483 StartY=46.995 StartZ=0 EndX=21.0483 EndY=60.995 EndZ=0
    g7: LineSegment StartX=21.0483 StartY=60.995 StartZ=0 EndX=16.0483 EndY=60.995 EndZ=0
    g8: Circle CenterX=31.0483 CenterY=33.495 CenterZ=0 NormalX=0 NormalY=0 NormalZ=1 AngleXU=0 Radius=4
  constraints (25):
    c: Vertical(g0)
    c: Coincident(g0,g1)
    c: Horizontal(g1)
    c: Coincident(g1,g2)
    c: Vertical(g2)
    c: Coincident(g2,g3)
    c: Horizontal(g3)
    c: Coincident(g3,g4)
    c: Vertical(g4)
    c: Coincident(g4,g5)
    c: Horizontal(g5)
    c: Coincident(g5,g6)
    c: Vertical(g6)
    c: Coincident(g6,g7)
    c: Coincident(g7,g0)
    c: Horizontal(g7)
    c: DistanceY(g0,g0) = 55
    c: DistanceX(g7,g7) = 5
    c: Equal(g7,g1)
    c: Radius(g8) = 4
    c: Distance(g8,g0) = 15
    c: Equal(g6,g2)
    c: Distance(g8,g4) = 13.5
    c: Distance(g8,g5) = 13.5
    c: Distance(g8,g3) = 13.5
FEATURE [Part::Extrusion] Extrude015  label="KP08 Z sup. direito"
  Base = -> Sketch015
  Dir = (0,0,13)
  DirMode = 0
  FaceMakerClass = Part::FaceMakerBullseye
  LengthFwd = 10
  LengthRev = 0
  Placement = pos=(1272,536.5,-97) rot=(0,0,1;3.14159rad)
  Solid = true
  Symmetric = false
FEATURE [Part::Box] Box049  label="Suporte fuso nema inf. esquerdo"
  AttacherType = Attacher::AttachEngine3D
  Height = 114
  Length = 6
  Placement = pos=(676,444,-676) rot=(0,0,1;0rad)
  Width = 120
FEATURE [Part::Box] Box050  label="Suporte fuso nema inf. direito"
  AttacherType = Attacher::AttachEngine3D
  Height = 114
  Length = 6
  Placement = pos=(1263,444,-676) rot=(0,0,1;0rad)
  Width = 120
FEATURE [Part::Box] Box051  label="Suporte fuso sup. direito"
  AttacherType = Attacher::AttachEngine3D
  Height = 20
  Length = 12
  Placement = pos=(1256.5,475,-102) rot=(0,0,1;0rad)
  Width = 56
FEATURE [Part::Box] Box052  label="Suporte fuso sup. esquerdo"
  AttacherType = Attacher::AttachEngine3D
  Height = 20
  Length = 12
  Placement = pos=(676,475,-102) rot=(0,0,1;0rad)
  Width = 56
FEATURE [Sketcher::SketchObject] Sketch016
  MapMode = 5
  Placement = pos=(42.5777,14,39) rot=(0.447214,-0.774597,-0.447214;1.82348rad)
  sketch-geometry (8):
    g0: LineSegment StartX=-123.305 StartY=6.07085 StartZ=0 EndX=-123.345 EndY=-1.16956 EndZ=0
    g1: LineSegment StartX=-123.345 StartY=-1.16956 StartZ=0 EndX=-100.407 EndY=-23.6651 EndZ=0
    g2: LineSegment StartX=-9.4672 StartY=-97.368 StartZ=0 EndX=-1.01841 EndY=-90.2813 EndZ=0
    g3: LineSegment StartX=-34.8682 StartY=6.09489 StartZ=0 EndX=-123.305 EndY=6.07085 EndZ=0
    g4: LineSegment StartX=-34.8682 StartY=6.09489 StartZ=0 EndX=-3.03674 EndY=-87.875 EndZ=0
    g5: LineSegment StartX=-3.03674 StartY=-87.875 StartZ=0 EndX=-1.01841 EndY=-90.2813 EndZ=0
    g6: LineSegment StartX=-100.407 StartY=-23.6651 StartZ=0 EndX=-15.5201 EndY=-91.5664 EndZ=0
    g7: LineSegment StartX=-15.5201 StartY=-91.5664 StartZ=0 EndX=-9.4672 EndY=-97.368 EndZ=0
  constraints (9):
    c: Coincident(g0,g1)
    c: Coincident(g3,g0)
    c: Coincident(g3,g4)
    c: Coincident(g4,g5)
    c: Coincident(g5,g2)
    c: Coincident(g1,g6)
    c: Coincident(g6,g7)
    c: Coincident(g7,g2)
    c: Perpendicular(g2,g5)
FEATURE [Sketcher::SketchObject] Sketch017
  MapMode = 5
  sketch-geometry (4):
    g0: LineSegment StartX=39.98 StartY=47.8377 StartZ=0 EndX=39.98 EndY=13.5387 EndZ=0
    g1: LineSegment StartX=39.98 StartY=13.5387 StartZ=0 EndX=127.229 EndY=13.5387 EndZ=0
    g2: LineSegment StartX=127.229 StartY=13.5387 StartZ=0 EndX=127.229 EndY=47.8377 EndZ=0
    g3: LineSegment StartX=127.229 StartY=47.8377 StartZ=0 EndX=39.98 EndY=47.8377 EndZ=0
  constraints (8):
    c: Coincident(g0,g1)
    c: Coincident(g1,g2)
    c: Coincident(g2,g3)
    c: Coincident(g3,g0)
    c: Perpendicular(g2,g1)
    c: Perpendicular(g3,g2)
    c: Perpendicular(g0,g3)
    c: Horizontal(g3)
FEATURE [Sketcher::SketchObject] Sketch018
  MapMode = 5
  sketch-geometry (4):
    g0: LineSegment StartX=39.5777 StartY=47.8687 StartZ=0 EndX=39.5777 EndY=34.8687 EndZ=0
    g1: LineSegment StartX=39.5777 StartY=34.8687 StartZ=0 EndX=127.578 EndY=34.8687 EndZ=0
    g2: LineSegment StartX=127.578 StartY=34.8687 StartZ=0 EndX=127.578 EndY=47.8687 EndZ=0
    g3: LineSegment StartX=127.578 StartY=47.8687 StartZ=0 EndX=39.5777 EndY=47.8687 EndZ=0
  constraints (10):
    c: Coincident(g0,g1)
    c: Coincident(g1,g2)
    c: Coincident(g2,g3)
    c: Coincident(g3,g0)
    c: Perpendicular(g2,g1)
    c: Perpendicular(g3,g2)
    c: Perpendicular(g0,g3)
    c: Horizontal(g3)
    c: DistanceY(g2,g2) = 13
    c: DistanceX(g3,g3) = 88
FEATURE [Sketcher::SketchObject] Sketch019
  MapMode = 5
  sketch-geometry (5):
    g0: LineSegment StartX=39.1898 StartY=122.876 StartZ=0 EndX=39.1898 EndY=34.8759 EndZ=0
    g1: LineSegment StartX=39.1898 StartY=34.8759 StartZ=0 EndX=127.19 EndY=34.8759 EndZ=0
    g2: LineSegment StartX=127.19 StartY=34.8759 StartZ=0 EndX=127.19 EndY=122.876 EndZ=0
    g3: LineSegment StartX=127.19 StartY=122.876 StartZ=0 EndX=39.1898 EndY=122.876 EndZ=0
    g4: Circle CenterX=83.1898 CenterY=78.8759 CenterZ=0 NormalX=0 NormalY=0 NormalZ=1 AngleXU=0 Radius=38
  constraints (13):
    c: Coincident(g0,g1)
    c: Coincident(g1,g2)
    c: Coincident(g2,g3)
    c: Coincident(g3,g0)
    c: Perpendicular(g2,g1)
    c: Perpendicular(g3,g2)
    c: Perpendicular(g0,g3)
    c: Horizontal(g3)
    c: DistanceY(g2,g2) = 88
    c: DistanceX(g3,g3) = 88
    c: Radius(g4) = 38
    c: DistanceY(g4,g0) = 44
    c: DistanceX(g0,g4) = 44
FEATURE [Mesh::Feature] hotend_3d_printer001  label="hotend-3d-printer001"
  Placement = pos=(939.5,443.5,-91) rot=(0,0,1;0rad)
FEATURE [Mesh::Feature] hotend_3d_printer  label="hotend-3d-printer"
  Placement = pos=(916,443.5,-91) rot=(0,0,1;0rad)
FEATURE [Sketcher::SketchObject] Sketch020
  MapMode = 5
  sketch-geometry (4):
    g0: LineSegment StartX=39.98 StartY=47.8377 StartZ=0 EndX=39.98 EndY=13.5387 EndZ=0
    g1: LineSegment StartX=39.98 StartY=13.5387 StartZ=0 EndX=127.229 EndY=13.5387 EndZ=0
    g2: LineSegment StartX=127.229 StartY=13.5387 StartZ=0 EndX=127.229 EndY=47.8377 EndZ=0
    g3: LineSegment StartX=127.229 StartY=47.8377 StartZ=0 EndX=39.98 EndY=47.8377 EndZ=0
  constraints (8):
    c: Coincident(g0,g1)
    c: Coincident(g1,g2)
    c: Coincident(g2,g3)
    c: Coincident(g3,g0)
    c: Perpendicular(g2,g1)
    c: Perpendicular(g3,g2)
    c: Perpendicular(g0,g3)
    c: Horizontal(g3)
FEATURE [Sketcher::SketchObject] Sketch021
  MapMode = 5
  sketch-geometry (4):
    g0: LineSegment StartX=39.5777 StartY=47.8687 StartZ=0 EndX=39.5777 EndY=34.8687 EndZ=0
    g1: LineSegment StartX=39.5777 StartY=34.8687 StartZ=0 EndX=127.578 EndY=34.8687 EndZ=0
    g2: LineSegment StartX=127.578 StartY=34.8687 StartZ=0 EndX=127.578 EndY=47.8687 EndZ=0
    g3: LineSegment StartX=127.578 StartY=47.8687 StartZ=0 EndX=39.5777 EndY=47.8687 EndZ=0
  constraints (10):
    c: Coincident(g0,g1)
    c: Coincident(g1,g2)
    c: Coincident(g2,g3)
    c: Coincident(g3,g0)
    c: Perpendicular(g2,g1)
    c: Perpendicular(g3,g2)
    c: Perpendicular(g0,g3)
    c: Horizontal(g3)
    c: DistanceY(g2,g2) = 13
    c: DistanceX(g3,g3) = 88
FEATURE [Sketcher::SketchObject] Sketch022
  MapMode = 5
  sketch-geometry (8):
    g0: LineSegment StartX=114.524 StartY=26.4586 StartZ=0 EndX=101.615 EndY=34.0979 EndZ=0
    g1: LineSegment StartX=101.615 StartY=34.0979 StartZ=0 EndX=109.153 EndY=46.8348 EndZ=0
    g2: LineSegment StartX=109.153 StartY=46.8348 StartZ=0 EndX=101.235 EndY=51.5202 EndZ=0
    g3: LineSegment StartX=101.235 StartY=51.5202 StartZ=0 EndX=107.296 EndY=61.7613 EndZ=0
    g4: LineSegment StartX=107.296 StartY=61.7613 StartZ=0 EndX=115.213 EndY=57.0759 EndZ=0
    g5: LineSegment StartX=115.213 StartY=57.0759 StartZ=0 EndX=122.751 EndY=69.8127 EndZ=0
    g6: LineSegment StartX=122.751 StartY=69.8127 StartZ=0 EndX=135.66 EndY=62.1734 EndZ=0
    g7: LineSegment StartX=135.66 StartY=62.1734 StartZ=0 EndX=114.524 EndY=26.4586 EndZ=0
  constraints (21):
    c: Coincident(g0,g1)
    c: Coincident(g1,g2)
    c: Coincident(g2,g3)
    c: Coincident(g3,g4)
    c: Coincident(g4,g5)
    c: Coincident(g5,g6)
    c: Coincident(g6,g7)
    c: Coincident(g7,g0)
    c: Equal(g2,g4)
    c: Equal(g1,g5)
    c: Perpendicular(g1,g2)
    c: Perpendicular(g2,g3)
    c: Perpendicular(g3,g4)
    c: Perpendicular(g5,g4)
    c: Perpendicular(g6,g5)
    c: Perpendicular(g7,g6)
    c: Perpendicular(g7,g0)
    c: Distance(g2,g3) = 11.9
    c: Distance(g2,g1) = 9.2
    c: Distance(g0,g1) = 14.8
    c: Distance(g0,g0) = 15
FEATURE [Sketcher::SketchObject] Sketch023
  MapMode = 5
  sketch-geometry (8):
    g0: LineSegment StartX=37.3535 StartY=63.0419 StartZ=0 EndX=50.4036 EndY=70.4376 EndZ=0
    g1: LineSegment StartX=50.4036 StartY=70.4376 StartZ=0 EndX=57.7007 EndY=57.5616 EndZ=0
    g2: LineSegment StartX=57.7007 StartY=57.5616 StartZ=0 EndX=65.7047 EndY=62.0976 EndZ=0
    g3: LineSegment StartX=65.7047 StartY=62.0976 StartZ=0 EndX=71.572 EndY=51.7446 EndZ=0
    g4: LineSegment StartX=71.572 StartY=51.7446 StartZ=0 EndX=63.5679 EndY=47.2085 EndZ=0
    g5: LineSegment StartX=63.5679 StartY=47.2085 StartZ=0 EndX=70.8651 EndY=34.3325 EndZ=0
    g6: LineSegment StartX=70.8651 StartY=34.3325 StartZ=0 EndX=57.815 EndY=26.9368 EndZ=0
    g7: LineSegment StartX=57.815 StartY=26.9368 StartZ=0 EndX=37.3535 EndY=63.0419 EndZ=0
  constraints (21):
    c: Coincident(g0,g1)
    c: Coincident(g1,g2)
    c: Coincident(g2,g3)
    c: Coincident(g3,g4)
    c: Coincident(g4,g5)
    c: Coincident(g5,g6)
    c: Coincident(g6,g7)
    c: Coincident(g7,g0)
    c: Equal(g2,g4)
    c: Equal(g1,g5)
    c: Perpendicular(g1,g2)
    c: Perpendicular(g2,g3)
    c: Perpendicular(g3,g4)
    c: Perpendicular(g5,g4)
    c: Perpendicular(g6,g5)
    c: Perpendicular(g7,g6)
    c: Perpendicular(g7,g0)
    c: Distance(g2,g3) = 11.9
    c: Distance(g2,g1) = 9.2
    c: Distance(g0,g1) = 14.8
    c: Distance(g0,g0) = 15
FEATURE [Sketcher::SketchObject] Sketch024
  MapMode = 5
  sketch-geometry (8):
    g0: LineSegment StartX=107.535 StartY=111.722 StartZ=0 EndX=107.501 EndY=96.7222 EndZ=0
    g1: LineSegment StartX=107.501 StartY=96.7222 StartZ=0 EndX=92.7007 EndY=96.7558 EndZ=0
    g2: LineSegment StartX=92.7007 StartY=96.7558 StartZ=0 EndX=92.6798 EndY=87.5559 EndZ=0
    g3: LineSegment StartX=92.6798 StartY=87.5559 StartZ=0 EndX=80.7798 EndY=87.5829 EndZ=0
    g4: LineSegment StartX=80.7798 StartY=87.5829 StartZ=0 EndX=80.8007 EndY=96.7829 EndZ=0
    g5: LineSegment StartX=80.8007 StartY=96.7829 StartZ=0 EndX=66.0008 EndY=96.8166 EndZ=0
    g6: LineSegment StartX=66.0008 StartY=96.8166 StartZ=0 EndX=66.0349 EndY=111.817 EndZ=0
    g7: LineSegment StartX=66.0349 StartY=111.817 StartZ=0 EndX=107.535 EndY=111.722 EndZ=0
  constraints (21):
    c: Coincident(g0,g1)
    c: Coincident(g1,g2)
    c: Coincident(g2,g3)
    c: Coincident(g3,g4)
    c: Coincident(g4,g5)
    c: Coincident(g5,g6)
    c: Coincident(g6,g7)
    c: Coincident(g7,g0)
    c: Equal(g2,g4)
    c: Equal(g1,g5)
    c: Perpendicular(g1,g2)
    c: Perpendicular(g2,g3)
    c: Perpendicular(g3,g4)
    c: Perpendicular(g5,g4)
    c: Perpendicular(g6,g5)
    c: Perpendicular(g7,g6)
    c: Perpendicular(g7,g0)
    c: Distance(g2,g3) = 11.9
    c: Distance(g2,g1) = 9.2
    c: Distance(g0,g1) = 14.8
    c: Distance(g0,g0) = 15
FEATURE [Part::Extrusion] Extrude017
  Base = -> Sketch016
  Dir = (-1,0,0)
  DirMode = 2
  FaceMakerClass = Part::FaceMakerBullseye
  LengthFwd = 7
  LengthRev = 0
  Placement = pos=(88,0,0) rot=(0,0,1;0rad)
  Solid = true
  Symmetric = false
FEATURE [Part::Extrusion] Extrude018
  Base = -> Sketch019
  Dir = (0,0,1)
  DirMode = 2
  FaceMakerClass = Part::FaceMakerBullseye
  LengthFwd = 7
  LengthRev = 0
  Placement = pos=(3,14,39) rot=(-1,0,0;0.523599rad)
  Solid = true
  Symmetric = false
FEATURE [Sketcher::SketchObject] Sketch025
  sketch-geometry (39):
    g0: LineSegment StartX=92.1382 StartY=71.478 StartZ=0 EndX=99.1382 EndY=59.3536 EndZ=0
    g1: LineSegment StartX=68.3387 StartY=30.9498 StartZ=0 EndX=82.3387 EndY=30.9498 EndZ=0
    g2: LineSegment StartX=59.14 StartY=71.8249 StartZ=0 EndX=52.14 EndY=59.7005 EndZ=0
    g3: LineSegment StartX=82.3387 StartY=30.9498 StartZ=0 EndX=83.7847 EndY=26.0283 EndZ=0
    g4: LineSegment StartX=83.7847 StartY=26.0283 StartZ=0 EndX=87.6579 EndY=23.7374 EndZ=0
    g5: LineSegment StartX=87.6579 StartY=23.7374 StartZ=0 EndX=92.6674 EndY=24.8409 EndZ=0
    g6: LineSegment StartX=92.6674 StartY=24.8409 StartZ=0 EndX=98.0127 EndY=33.8785 EndZ=0
    g7: LineSegment StartX=98.0127 StartY=33.8785 StartZ=0 EndX=90.2662 EndY=38.4602 EndZ=0
    g8: LineSegment StartX=90.2662 StartY=38.4602 StartZ=0 EndX=96.3751 EndY=48.7888 EndZ=0
    g9: LineSegment StartX=96.3751 StartY=48.7888 StartZ=0 EndX=104.122 EndY=44.2072 EndZ=0
    g10: LineSegment StartX=104.122 StartY=44.2072 StartZ=0 EndX=109.467 EndY=53.2447 EndZ=0
    g11: LineSegment StartX=109.467 StartY=53.2447 StartZ=0 EndX=108.021 EndY=58.1663 EndZ=0
    g12: LineSegment StartX=108.021 StartY=58.1663 StartZ=0 EndX=104.148 EndY=60.4571 EndZ=0
    g13: LineSegment StartX=104.148 StartY=60.4571 StartZ=0 EndX=99.1382 EndY=59.3536 EndZ=0
    g14: LineSegment StartX=92.1382 StartY=71.478 StartZ=0 EndX=95.6774 EndY=75.191 EndZ=0
    g15: LineSegment StartX=95.6774 StartY=75.191 StartZ=0 EndX=95.7247 EndY=79.6908 EndZ=0
    g16: LineSegment StartX=95.7247 StartY=79.6908 StartZ=0 EndX=92.2644 EndY=83.4773 EndZ=0
    g17: LineSegment StartX=92.2644 StartY=83.4773 StartZ=0 EndX=81.7649 EndY=83.5877 EndZ=0
    g18: LineSegment StartX=81.7649 StartY=83.5877 StartZ=0 EndX=81.6703 EndY=74.5882 EndZ=0
    g19: LineSegment StartX=81.6703 StartY=74.5882 StartZ=0 EndX=69.671 EndY=74.7143 EndZ=0
    g20: LineSegment StartX=69.671 StartY=74.7143 StartZ=0 EndX=69.7656 EndY=83.7138 EndZ=0
    g21: LineSegment StartX=69.7656 StartY=83.7138 StartZ=0 EndX=59.2662 EndY=83.8242 EndZ=0
    g22: LineSegment StartX=59.2662 StartY=83.8242 StartZ=0 EndX=55.727 EndY=80.1112 EndZ=0
    g23: LineSegment StartX=55.727 StartY=80.1112 StartZ=0 EndX=55.6796 EndY=75.6115 EndZ=0
    g24: LineSegment StartX=55.6796 StartY=75.6115 StartZ=0 EndX=59.14 EndY=71.8249 EndZ=0
    g25: LineSegment StartX=52.14 StartY=59.7005 StartZ=0 EndX=47.1537 EndY=60.9041 EndZ=0
    g26: LineSegment StartX=47.1537 StartY=60.9041 StartZ=0 EndX=43.2331 EndY=58.6952 EndZ=0
    g27: LineSegment StartX=43.2331 StartY=58.6952 StartZ=0 EndX=41.6889 EndY=53.8036 EndZ=0
    g28: LineSegment StartX=41.6889 StartY=53.8036 StartZ=0 EndX=46.8412 EndY=44.6589 EndZ=0
    g29: LineSegment StartX=46.8412 StartY=44.6589 StartZ=0 EndX=54.6823 EndY=49.0767 EndZ=0
    g30: LineSegment StartX=54.6823 StartY=49.0767 StartZ=0 EndX=60.5727 EndY=38.6219 EndZ=0
    g31: LineSegment StartX=60.5727 StartY=38.6219 StartZ=0 EndX=52.7316 EndY=34.2041 EndZ=0
    g32: LineSegment StartX=52.7316 StartY=34.2041 StartZ=0 EndX=57.8876 EndY=25.0529 EndZ=0
    g33: LineSegment StartX=57.8876 StartY=25.0529 StartZ=0 EndX=62.874 EndY=23.8493 EndZ=0
    g34: LineSegment StartX=62.874 StartY=23.8493 StartZ=0 EndX=66.7945 EndY=26.0582 EndZ=0
    g35: LineSegment StartX=66.7945 StartY=26.0582 StartZ=0 EndX=68.3387 EndY=30.9498 EndZ=0
    g36: Circle CenterX=76.5882 CenterY=60.6409 CenterZ=0 NormalX=0 NormalY=0 NormalZ=1 AngleXU=0 Radius=5
    g37: Circle CenterX=64.202 CenterY=52.7706 CenterZ=0 NormalX=0 NormalY=0 NormalZ=1 AngleXU=0 Radius=6.5
    g38: Circle CenterX=88.2006 CenterY=52.5183 CenterZ=0 NormalX=0 NormalY=0 NormalZ=1 AngleXU=0 Radius=6.5
  constraints (112):
    c: Angle(g0,g1) = 1.0472
    c: Equal(g2,g0)
    c: Equal(g0,g1)
    c: Distance(g2,g2) = 14
    c: Horizontal(g1)
    c: Angle(g1,g2) = 1.0472
    c: Distance(g0,g1) = 33
    c: Distance(g0,g2) = 33
    c: Distance(g2,g1) = 33
    c: Coincident(g1,g3)
    c: Coincident(g3,g4)
    c: Coincident(g4,g5)
    c: Coincident(g5,g6)
    c: Coincident(g6,g7)
    c: Coincident(g7,g8)
    c: Coincident(g8,g9)
    c: Coincident(g9,g10)
    c: Coincident(g10,g11)
    c: Coincident(g11,g12)
    c: Coincident(g12,g13)
    c: Coincident(g13,g0)
    c: Equal(g10,g6)
    c: Perpendicular(g8,g9)
    c: Perpendicular(g7,g8)
    c: Perpendicular(g10,g9)
    c: Perpendicular(g6,g7)
    c: Equal(g7,g9)
    c: Distance(g7,g6) = 9
    c: Distance(g0,g10) = 12
    c: Distance(g1,g5) = 12
    c: Distance(g11,g9) = 14
    c: Distance(g12,g9) = 14
    c: Distance(g5,g10) = 33
    c: Distance(g4,g7) = 14
    c: Distance(g3,g7) = 14
    c: Equal(g4,g12)
    c: Distance(g3,g4) = 4.5
    c: Equal(g4,g12)
    c: Equal(g5,g3)
    c: Equal(g3,g11)
    c: Equal(g11,g13)
    c: Distance(g8,g7) = 12
    c: Coincident(g0,g14)
    c: Coincident(g14,g15)
    c: Coincident(g15,g16)
    c: Coincident(g16,g17)
    c: Coincident(g17,g18)
    c: Coincident(g18,g19)
    c: Coincident(g19,g20)
    c: Coincident(g20,g21)
    c: Coincident(g21,g22)
    c: Coincident(g22,g23)
    c: Coincident(g23,g24)
    c: Coincident(g24,g2)
    c: Distance(g16,g21) = 33
    c: Distance(g19,g18) = 12
    c: Perpendicular(g20,g19)
    c: Perpendicular(g18,g19)
    c: Perpendicular(g18,g17)
    c: Perpendicular(g21,g20)
    c: Equal(g18,g20)
    c: Equal(g21,g17)
    c: Distance(g18,g17) = 9
    c: Distance(g0,g16) = 12
    c: Distance(g2,g21) = 12
    c: Distance(g22,g20) = 14
    c: Distance(g23,g20) = 14
    c: Distance(g15,g18) = 14
    c: Distance(g14,g18) = 14
    c: Equal(g14,g16)
    c: Equal(g16,g22)
    c: Equal(g22,g24)
    c: Equal(g23,g15)
    c: Distance(g23,g22) = 4.5
    c: Coincident(g2,g25)
    c: Coincident(g25,g26)
    c: Coincident(g26,g27)
    c: Coincident(g27,g28)
    c: Coincident(g28,g29)
    c: Coincident(g29,g30)
    c: Coincident(g30,g31)
    c: Coincident(g31,g32)
    c: Coincident(g32,g33)
    c: Coincident(g33,g34)
    c: Coincident(g34,g35)
    c: Coincident(g35,g1)
    c: Distance(g28,g29) = 9
    c: Equal(g29,g31)
    c: Distance(g29,g30) = 12
    c: Perpendicular(g30,g29)
    c: Perpendicular(g31,g30)
    c: Perpendicular(g29,g28)
    c: Perpendicular(g32,g31)
    c: Distance(g27,g32) = 33
    c: Distance(g2,g27) = 12
    c: Distance(g32,g1) = 12
    c: Distance(g26,g29) = 14
    c: Distance(g25,g29) = 14
    c: Distance(g34,g31) = 14
    c: Distance(g33,g31) = 14
    c: Equal(g26,g34)
    c: Distance(g25,g26) = 4.5
    c: Equal(g25,g27)
    c: Equal(g27,g33)
    c: Equal(g33,g35)
    c: Radius(g37) = 6.5
    c: Radius(g38) = 6.5
    c: Radius(g36) = 5
    c: Distance(g36,g19) = 14
    c: Distance(g37,g38) = 24
    c: Distance(g38,g17) = 31
    c: Distance(g37,g21) = 31
FEATURE [Sketcher::SketchObject] Sketch026
  sketch-geometry (8):
    g0: LineSegment StartX=64.0547 StartY=96.1652 StartZ=0 EndX=64.0547 EndY=32.1652 EndZ=0
    g1: LineSegment StartX=64.0547 StartY=32.1652 StartZ=0 EndX=121.055 EndY=32.1652 EndZ=0
    g2: LineSegment StartX=121.055 StartY=32.1652 StartZ=0 EndX=121.055 EndY=41.1652 EndZ=0
    g3: LineSegment StartX=121.055 StartY=41.1652 StartZ=0 EndX=74.0547 EndY=41.1652 EndZ=0
    g4: LineSegment StartX=74.0547 StartY=41.1652 StartZ=0 EndX=74.0547 EndY=87.1652 EndZ=0
    g5: LineSegment StartX=74.0547 StartY=87.1652 StartZ=0 EndX=121.055 EndY=87.1652 EndZ=0
    g6: LineSegment StartX=121.055 StartY=87.1652 StartZ=0 EndX=121.055 EndY=96.1652 EndZ=0
    g7: LineSegment StartX=121.055 StartY=96.1652 StartZ=0 EndX=64.0547 EndY=96.1652 EndZ=0
  constraints (22):
    c: Vertical(g0)
    c: Coincident(g0,g1)
    c: Horizontal(g1)
    c: Coincident(g1,g2)
    c: Vertical(g2)
    c: Coincident(g2,g3)
    c: Horizontal(g3)
    c: Coincident(g3,g4)
    c: Vertical(g4)
    c: Coincident(g4,g5)
    c: Horizontal(g5)
    c: Coincident(g5,g6)
    c: Coincident(g6,g7)
    c: Coincident(g7,g0)
    c: Horizontal(g7)
    c: Equal(g7,g1)
    c: Equal(g5,g3)
    c: Equal(g6,g2)
    c: DistanceY(g0,g0) = 64
    c: DistanceX(g7,g7) = 57
    c: DistanceX(g5,g5) = 47
    c: DistanceY(g4,g4) = 46
FEATURE [Part::Extrusion] Extrude016  label="PlateX_01"
  Base = -> Sketch026
  Dir = (0,0,1)
  DirMode = 2
  FaceMakerClass = Part::FaceMakerBullseye
  LengthFwd = 88
  LengthRev = 0
  Placement = pos=(173,108,74) rot=(0.57735,-0.57735,0.57735;4.18879rad)
  Solid = true
  Symmetric = false
FEATURE [Sketcher::SketchObject] Sketch027
  sketch-geometry (8):
    g0: LineSegment StartX=40.1304 StartY=23.3379 StartZ=0 EndX=40.1304 EndY=69.2379 EndZ=0
    g1: LineSegment StartX=40.1304 StartY=69.2379 StartZ=0 EndX=41.1304 EndY=69.2379 EndZ=0
    g2: LineSegment StartX=41.1304 StartY=69.2379 StartZ=0 EndX=41.1304 EndY=78.2379 EndZ=0
    g3: LineSegment StartX=41.1304 StartY=78.2379 StartZ=0 EndX=51.1304 EndY=78.2379 EndZ=0
    g4: LineSegment StartX=51.1304 StartY=78.2379 StartZ=0 EndX=51.1304 EndY=14.3379 EndZ=0
    g5: LineSegment StartX=51.1304 StartY=14.3379 StartZ=0 EndX=41.1304 EndY=14.3379 EndZ=0
    g6: LineSegment StartX=41.1304 StartY=14.3379 StartZ=0 EndX=41.1304 EndY=23.3379 EndZ=0
    g7: LineSegment StartX=41.1304 StartY=23.3379 StartZ=0 EndX=40.1304 EndY=23.3379 EndZ=0
  constraints (23):
    c: Vertical(g0)
    c: Coincident(g0,g1)
    c: Horizontal(g1)
    c: Coincident(g1,g2)
    c: Coincident(g2,g3)
    c: Horizontal(g3)
    c: Coincident(g3,g4)
    c: Coincident(g4,g5)
    c: Coincident(g5,g6)
    c: Vertical(g6)
    c: Coincident(g6,g7)
    c: Coincident(g7,g0)
    c: Vertical(g2)
    c: Vertical(g4)
    c: Horizontal(g5)
    c: Horizontal(g7)
    c: Equal(g2,g6)
    c: Equal(g3,g5)
    c: Equal(g1,g7)
    c: DistanceY(g0,g0) = 45.9
    c: DistanceY(g2,g2) = 9
    c: DistanceX(g7,g7) = 1
    c: DistanceX(g3,g3) = 10
FEATURE [Part::Extrusion] Extrude019
  Base = -> Sketch023
  Dir = (0,0,1)
  DirMode = 2
  FaceMakerClass = Part::FaceMakerBullseye
  LengthFwd = 19
  LengthRev = 0
  Solid = true
  Symmetric = false
FEATURE [Part::Extrusion] Extrude020
  Base = -> Sketch018
  Dir = (0,0,1)
  DirMode = 2
  FaceMakerClass = Part::FaceMakerBullseye
  LengthFwd = 64
  LengthRev = 0
  Placement = pos=(3,0,19) rot=(0,0,1;0rad)
  Solid = true
  Symmetric = false
FEATURE [Part::Extrusion] Extrude021
  Base = -> Sketch017
  Dir = (0,0,1)
  DirMode = 2
  FaceMakerClass = Part::FaceMakerBullseye
  LengthFwd = 10
  LengthRev = 0
  Placement = pos=(3,0,9) rot=(0,0,1;0rad)
  Solid = true
  Symmetric = false
FEATURE [Part::Extrusion] Extrude022
  Base = -> Sketch024
  Dir = (0,0,1)
  DirMode = 2
  FaceMakerClass = Part::FaceMakerBullseye
  LengthFwd = 35
  LengthRev = 0
  Solid = true
  Symmetric = false
FEATURE [Part::Extrusion] Extrude023
  Base = -> Sketch021
  Dir = (0,0,1)
  DirMode = 2
  FaceMakerClass = Part::FaceMakerBullseye
  LengthFwd = 64
  LengthRev = 0
  Placement = pos=(3,0,19) rot=(0,0,1;0rad)
  Solid = true
  Symmetric = false
FEATURE [Part::Extrusion] Extrude024
  Base = -> Sketch020
  Dir = (0,0,1)
  DirMode = 2
  FaceMakerClass = Part::FaceMakerBullseye
  LengthFwd = 10
  LengthRev = 0
  Placement = pos=(3,0,9) rot=(0,0,1;0rad)
  Solid = true
  Symmetric = false
FEATURE [Part::Extrusion] Extrude025
  Base = -> Sketch022
  Dir = (0,0,1)
  DirMode = 2
  FaceMakerClass = Part::FaceMakerBullseye
  LengthFwd = 19
  LengthRev = 0
  Solid = true
  Symmetric = false
FEATURE [Part::MultiFuse] Fusion  label="Suporte1"
  Placement = pos=(303.5,11,-42) rot=(0,0,1;3.14159rad)
  Shapes = -> [Extrude023,Extrude024,Extrude025,Extrude019,Extrude022]
FEATURE [Part::Extrusion] Extrude027  label="PlateX_02"
  Base = -> Sketch027
  Dir = (0,0,1)
  DirMode = 2
  FaceMakerClass = Part::FaceMakerBullseye
  LengthFwd = 88
  LengthRev = 0
  Placement = pos=(173,28,56) rot=(0.57735,-0.57735,0.57735;4.18879rad)
  Solid = true
  Symmetric = false
FEATURE [Part::Box] Box053  label="Mgn12h inferior"
  AttacherType = Attacher::AttachEngine3D
  Height = 13
  Length = 47.55
  Placement = pos=(193,-3,-13) rot=(0,0,1;0rad)
  Width = 27.1
FEATURE [Part::Box] Box002  label="Rail superior"
  AttacherType = Attacher::AttachEngine3D
  Height = 7.8
  Length = 400
  Placement = pos=(57,4,20) rot=(0,0,1;0rad)
  Width = 12.2
FEATURE [Part::Box] Box013  label="Mgn12h superior"
  AttacherType = Attacher::AttachEngine3D
  Height = 13
  Length = 47.55
  Placement = pos=(193,-3,20) rot=(0,0,1;0rad)
  Width = 27.1
FEATURE [Part::Box] Box004  label="Rail inferior"
  AttacherType = Attacher::AttachEngine3D
  Height = 7.8
  Length = 400
  Placement = pos=(57,4,-7.8) rot=(0,0,1;0rad)
  Width = 12.2
FEATURE [Part::Box] Box054  label="vSlot2020"
  AttacherType = Attacher::AttachEngine3D
  Height = 20
  Length = 660
  Placement = pos=(-70,0.5,0) rot=(0,0,1;0rad)
  Width = 20
FEATURE [Part::Extrusion] Extrude028  label="SuporteDelta"
  Base = -> Sketch025
  Dir = (0,0,1)
  DirMode = 2
  FaceMakerClass = Part::FaceMakerBullseye
  LengthFwd = 8
  LengthRev = 0
  Placement = pos=(292,-2,-40) rot=(0,0,1;3.14159rad)
  Solid = true
  Symmetric = false
FEATURE [Sketcher::SketchObject] Sketch028
  MapMode = 5
  Placement = pos=(42.5777,14,39) rot=(0.447214,-0.774597,-0.447214;1.82348rad)
  sketch-geometry (8):
    g0: LineSegment StartX=-123.305 StartY=6.07085 StartZ=0 EndX=-123.345 EndY=-1.16956 EndZ=0
    g1: LineSegment StartX=-123.345 StartY=-1.16956 StartZ=0 EndX=-100.407 EndY=-23.6651 EndZ=0
    g2: LineSegment StartX=-9.4672 StartY=-97.368 StartZ=0 EndX=-1.01841 EndY=-90.2813 EndZ=0
    g3: LineSegment StartX=-34.8682 StartY=6.09489 StartZ=0 EndX=-123.305 EndY=6.07085 EndZ=0
    g4: LineSegment StartX=-34.8682 StartY=6.09489 StartZ=0 EndX=-3.03674 EndY=-87.875 EndZ=0
    g5: LineSegment StartX=-3.03674 StartY=-87.875 StartZ=0 EndX=-1.01841 EndY=-90.2813 EndZ=0
    g6: LineSegment StartX=-100.407 StartY=-23.6651 StartZ=0 EndX=-15.5201 EndY=-91.5664 EndZ=0
    g7: LineSegment StartX=-15.5201 StartY=-91.5664 StartZ=0 EndX=-9.4672 EndY=-97.368 EndZ=0
  constraints (9):
    c: Coincident(g0,g1)
    c: Coincident(g3,g0)
    c: Coincident(g3,g4)
    c: Coincident(g4,g5)
    c: Coincident(g5,g2)
    c: Coincident(g1,g6)
    c: Coincident(g6,g7)
    c: Coincident(g7,g2)
    c: Perpendicular(g2,g5)
FEATURE [Part::Extrusion] Extrude026
  Base = -> Sketch028
  Dir = (-1,0,0)
  DirMode = 2
  FaceMakerClass = Part::FaceMakerBullseye
  LengthFwd = 7
  LengthRev = 0
  Placement = pos=(7,0,0) rot=(0,0,1;0rad)
  Solid = true
  Symmetric = false
FEATURE [Part::MultiFuse] Fusion001  label="Suporte2"
  Placement = pos=(130,10,-42) rot=(0,0,1;0rad)
  Shapes = -> [Extrude020,Extrude026,Extrude021,Extrude017,Extrude018]
FEATURE [Part::MultiFuse] Fusion002
  Placement = pos=(712,498,-52) rot=(0,0,1;0rad)
  Shapes = -> [Fusion001,Extrude016,Extrude027,Extrude028,Box054,Box004,Box053,Box002,Box013,Fusion]
FEATURE [App::DocumentObjectGroup] Group  label="Eixo X"
  Group = -> [hotend_3d_printer,hotend_3d_printer001,Fusion002]
FEATURE [Part::Box] Box055  label="HotBed 400x400"
  AttacherType = Attacher::AttachEngine3D
  Height = 5
  Length = 400
  Placement = pos=(769,298,-236) rot=(0,0,1;0rad)
  Width = 400
FEATURE [Part::Box] Box056  label="HotBed 200x200"
  AttacherType = Attacher::AttachEngine3D
  Height = 5
  Length = 200
  Placement = pos=(869,398,-231) rot=(0,0,1;0rad)
  Width = 200
FEATURE [Part::Box] Box057  label="Vslot suporte esquerdo"
  AttacherType = Attacher::AttachEngine3D
  Height = 20
  Length = 20
  Placement = pos=(717,261,-245) rot=(0,0,1;0rad)
  Width = 450
FEATURE [Part::Box] Box058  label="Vslot suporte direito"
  AttacherType = Attacher::AttachEngine3D
  Height = 20
  Length = 20
  Placement = pos=(1207,261,-245) rot=(0,0,1;0rad)
  Width = 450
